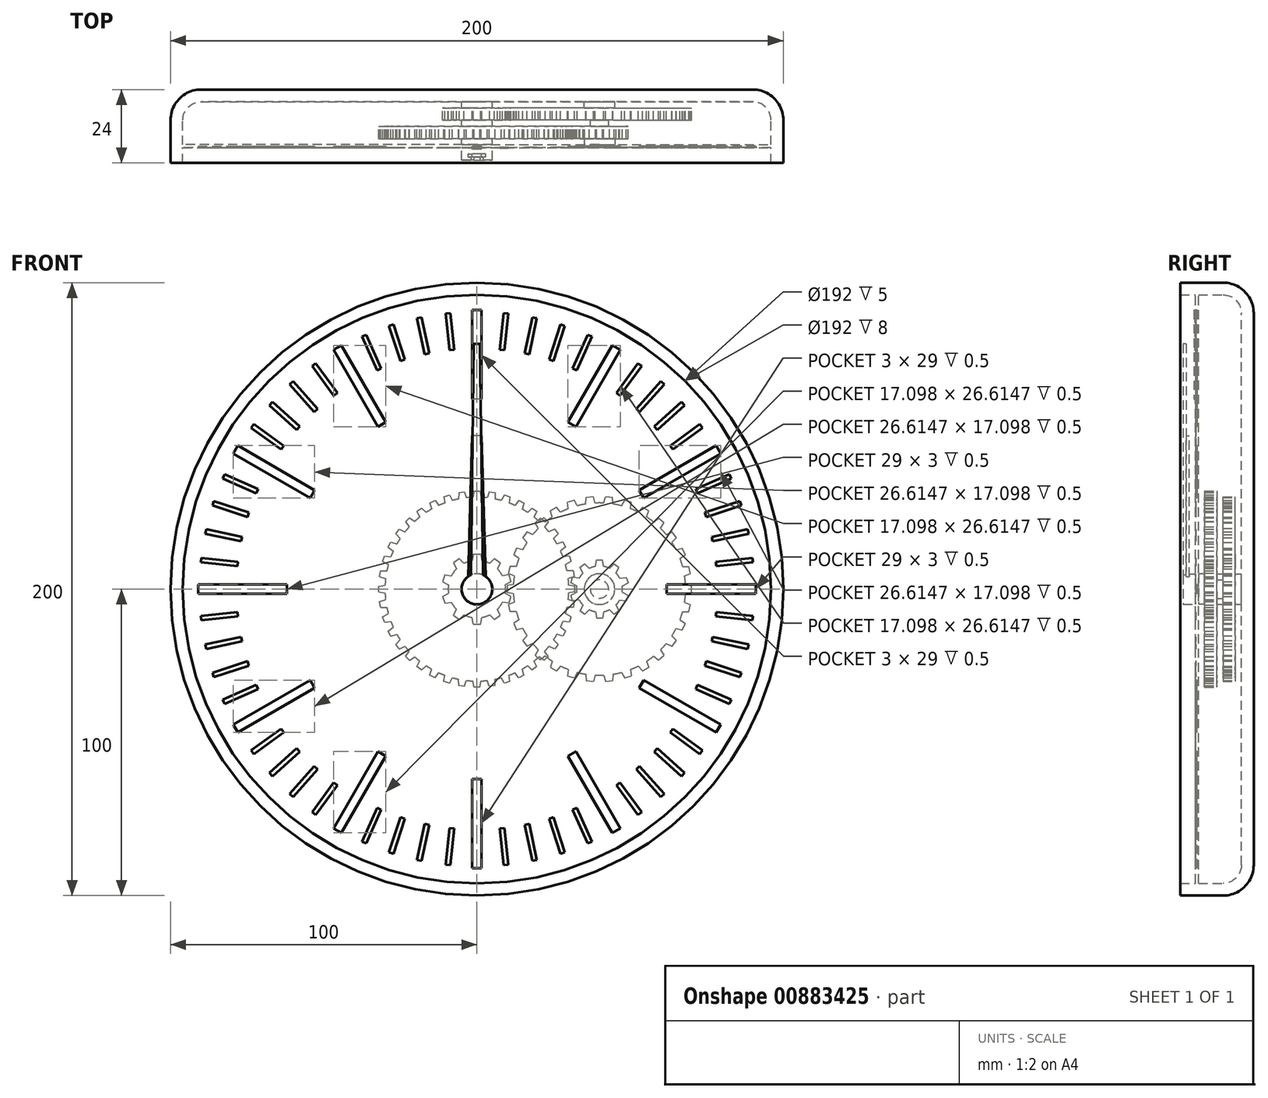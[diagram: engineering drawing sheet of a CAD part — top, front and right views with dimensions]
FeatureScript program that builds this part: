
annotation { "Feature Type Name" : "Feature", "Feature Type Description" : "" }
export const myFeature = defineFeature(function(context is Context, id is Id, definition is map)
    precondition{}
    {
        {
            var Q0;
            Q0=qCreatedBy(makeId("Front.planeOp"),FACE);
            var sketch = newSketch(context, id + "F0", { "sketchPlane" : qUnion([Q0])});
            skCircle(sketch, "E0", {"center": v(0, 0) * mm, "radius": 100 * mm});
            skSolve(sketch);
        }
        {
            var Q0;
            Q0 = qSketchRegion(id + "F0", true);
            extrude(context, id + "F1", {"entities" : qUnion([Q0]), "depth" : 24 * mm, "offsetDistance" : 25 * mm});
        }
        {
            var Q0;
            Q0=makeQuery(id+"F1.opExtrude","CAP_EDGE",EDGE,{"disambiguationData":[OSD([sQuery(id+"F0.wireOp",EDGE,"E0")])],"isStart":true});
            fillet(context, id + "F2", {"entities" : qUnion([Q0]), "radius" : 10 * mm, "tangentPropagation" : true, "allowEdgeOverflow" : false});
        }
        {
            var Q0;
            Q0=makeQuery(id+"F1.opExtrude","CAP_FACE",FACE,{"disambiguationData":[OSD([sQuery(id+"F0.wireOp",EDGE,"E0")])],"isStart":false});
            shell(context, id + "F3", {"entities" : qUnion([Q0]), "thickness" : 4 * mm});
        }
        {
            var Q0;
            {var subQ0=sQuery(id+"F0.wireOp",EDGE,"E0");Q0=makeQuery(id+"F3.opShell","OFFSET_FACE",FACE,{"disambiguationData":[OSD([subQ0]),TDD([makeQuery(id+"F1.opExtrude","CAP_FACE",FACE,{"disambiguationData":[OSD([subQ0])],"isStart":true})])]});}
            var sketch = newSketch(context, id + "F4", { "sketchPlane" : qUnion([Q0])});
            skCircle(sketch, "E1", {"center": v(0, 0) * mm, "radius": 3 * mm});
            skCircle(sketch, "E2", {"center": v(0, 0) * mm, "radius": 5 * mm});
            skCircle(sketch, "E3", {"center": v(40, 0) * mm, "radius": 3 * mm});
            skCircle(sketch, "E4", {"center": v(40, 0) * mm, "radius": 5 * mm});
            skSolve(sketch);
        }
        {
            var Q0;
            Q0 = qSketchRegion(id + "F4", true);
            extrude(context, id + "F5", {"entities" : qUnion([Q0]), "operationType" : NewBodyOperationType.ADD, "depth" : 2 * mm, "offsetDistance" : 25 * mm});
        }
        {
            var Q0;
            {var subQ0=sQuery(id+"F0.wireOp",EDGE,"E0");Q0=makeQuery(id+"F5.boolean.opBoolean","SPLIT",FACE,{"disambiguationData":[TD([makeQuery(id+"F5.opExtrude","SWEPT_FACE",FACE,{"disambiguationData":[OSD([sQuery(id+"F4.wireOp",EDGE,"E1")])]})])],"derivedFrom":makeQuery(id+"F3.opShell","OFFSET_FACE",FACE,{"disambiguationData":[OSD([subQ0]),TDD([makeQuery(id+"F1.opExtrude","CAP_FACE",FACE,{"disambiguationData":[OSD([subQ0])],"isStart":true})])]})});}
            extrude(context, id + "F6", {"entities" : qUnion([Q0]), "depth" : 19 * mm, "offsetDistance" : 25 * mm});
        }
        {
            var Q0;
            {var subQ0=sQuery(id+"F0.wireOp",EDGE,"E0");Q0=makeQuery(id+"F5.boolean.opBoolean","SPLIT",FACE,{"disambiguationData":[TD([makeQuery(id+"F5.opExtrude","SWEPT_FACE",FACE,{"disambiguationData":[OSD([sQuery(id+"F4.wireOp",EDGE,"E3")])]})])],"derivedFrom":makeQuery(id+"F3.opShell","OFFSET_FACE",FACE,{"disambiguationData":[OSD([subQ0]),TDD([makeQuery(id+"F1.opExtrude","CAP_FACE",FACE,{"disambiguationData":[OSD([subQ0])],"isStart":true})])]})});}
            extrude(context, id + "F7", {"entities" : qUnion([Q0]), "depth" : 8 * mm, "offsetDistance" : 25 * mm});
        }
        {
            var Q0;
            Q0=makeQuery(id+"F5.opExtrude","CAP_FACE",FACE,{"disambiguationData":[OSD([sQuery(id+"F4.wireOp",EDGE,"E1"),sQuery(id+"F4.wireOp",EDGE,"E2")])],"isStart":false});
            var sketch = newSketch(context, id + "F8", { "sketchPlane" : qUnion([Q0])});
            skCircle(sketch, "E5", {"center": v(0, 0) * mm, "radius": 9.38 * mm});
            skLineSegment(sketch, "E6", {"start": v(0, 11.38) * mm, "end": v(1.18, 11.38) * mm});
            skLineSegment(sketch, "E7", {"start": v(1.18, 11.38) * mm, "end": v(1.55, 9.25) * mm});
            skLineSegment(sketch, "E8.MirrorCS", {"start": v(0, 11.38) * mm, "end": v(-1.18, 11.38) * mm});
            skLineSegment(sketch, "E9.MirrorCS", {"start": v(-1.18, 11.38) * mm, "end": v(-1.55, 9.25) * mm});
            skLineSegment(sketch, "E10.1.0", {"start": v(-7.64, 8.51) * mm, "end": v(-6.7, 6.57) * mm});
            skLineSegment(sketch, "E10.1.1", {"start": v(-6.69, 9.2) * mm, "end": v(-7.64, 8.51) * mm});
            skLineSegment(sketch, "E10.1.2", {"start": v(-6.69, 9.2) * mm, "end": v(-5.73, 9.9) * mm});
            skLineSegment(sketch, "E10.1.3", {"start": v(-5.73, 9.9) * mm, "end": v(-4.18, 8.4) * mm});
            skLineSegment(sketch, "E10.2.0", {"start": v(-11.18, 2.4) * mm, "end": v(-9.27, 1.38) * mm});
            skLineSegment(sketch, "E10.2.1", {"start": v(-10.82, 3.52) * mm, "end": v(-11.18, 2.4) * mm});
            skLineSegment(sketch, "E10.2.2", {"start": v(-10.82, 3.52) * mm, "end": v(-10.45, 4.64) * mm});
            skLineSegment(sketch, "E10.2.3", {"start": v(-10.45, 4.64) * mm, "end": v(-8.31, 4.33) * mm});
            skLineSegment(sketch, "E11.2.3.0", {"start": v(-10.45, -4.64) * mm, "end": v(-8.31, -4.33) * mm});
            skLineSegment(sketch, "E11.3.3.0", {"start": v(-10.82, -3.52) * mm, "end": v(-10.45, -4.64) * mm});
            skLineSegment(sketch, "E11.6.3.0", {"start": v(-10.82, -3.52) * mm, "end": v(-11.18, -2.4) * mm});
            skLineSegment(sketch, "E11.9.3.0", {"start": v(-11.18, -2.4) * mm, "end": v(-9.27, -1.38) * mm});
            skLineSegment(sketch, "E11.2.4.0", {"start": v(-5.73, -9.9) * mm, "end": v(-4.18, -8.4) * mm});
            skLineSegment(sketch, "E11.3.4.0", {"start": v(-6.69, -9.2) * mm, "end": v(-5.73, -9.9) * mm});
            skLineSegment(sketch, "E11.6.4.0", {"start": v(-6.69, -9.2) * mm, "end": v(-7.64, -8.51) * mm});
            skLineSegment(sketch, "E11.9.4.0", {"start": v(-7.64, -8.51) * mm, "end": v(-6.7, -6.57) * mm});
            skLineSegment(sketch, "E11.2.5.0", {"start": v(1.18, -11.38) * mm, "end": v(1.55, -9.25) * mm});
            skLineSegment(sketch, "E11.3.5.0", {"start": v(0, -11.38) * mm, "end": v(1.18, -11.38) * mm});
            skLineSegment(sketch, "E11.6.5.0", {"start": v(0, -11.38) * mm, "end": v(-1.18, -11.38) * mm});
            skLineSegment(sketch, "E11.9.5.0", {"start": v(-1.18, -11.38) * mm, "end": v(-1.55, -9.25) * mm});
            skLineSegment(sketch, "E11.2.6.0", {"start": v(7.64, -8.51) * mm, "end": v(6.7, -6.57) * mm});
            skLineSegment(sketch, "E11.3.6.0", {"start": v(6.69, -9.2) * mm, "end": v(7.64, -8.51) * mm});
            skLineSegment(sketch, "E11.6.6.0", {"start": v(6.69, -9.2) * mm, "end": v(5.73, -9.9) * mm});
            skLineSegment(sketch, "E11.9.6.0", {"start": v(5.73, -9.9) * mm, "end": v(4.18, -8.4) * mm});
            skLineSegment(sketch, "E11.2.7.0", {"start": v(11.18, -2.4) * mm, "end": v(9.27, -1.38) * mm});
            skLineSegment(sketch, "E11.3.7.0", {"start": v(10.82, -3.52) * mm, "end": v(11.18, -2.4) * mm});
            skLineSegment(sketch, "E11.6.7.0", {"start": v(10.82, -3.52) * mm, "end": v(10.45, -4.64) * mm});
            skLineSegment(sketch, "E11.9.7.0", {"start": v(10.45, -4.64) * mm, "end": v(8.31, -4.33) * mm});
            skLineSegment(sketch, "E11.2.8.0", {"start": v(10.45, 4.64) * mm, "end": v(8.31, 4.33) * mm});
            skLineSegment(sketch, "E11.3.8.0", {"start": v(10.82, 3.52) * mm, "end": v(10.45, 4.64) * mm});
            skLineSegment(sketch, "E11.6.8.0", {"start": v(10.82, 3.52) * mm, "end": v(11.18, 2.4) * mm});
            skLineSegment(sketch, "E11.9.8.0", {"start": v(11.18, 2.4) * mm, "end": v(9.27, 1.38) * mm});
            skLineSegment(sketch, "E11.2.9.0", {"start": v(5.73, 9.9) * mm, "end": v(4.18, 8.4) * mm});
            skLineSegment(sketch, "E11.3.9.0", {"start": v(6.69, 9.2) * mm, "end": v(5.73, 9.9) * mm});
            skLineSegment(sketch, "E11.6.9.0", {"start": v(6.69, 9.2) * mm, "end": v(7.64, 8.51) * mm});
            skLineSegment(sketch, "E11.9.9.0", {"start": v(7.64, 8.51) * mm, "end": v(6.7, 6.57) * mm});
            skSolve(sketch);
        }
        {
            var Q0;
            Q0 = qSketchRegion(id + "F8", true);
            extrude(context, id + "F9", {"entities" : qUnion([Q0]), "operationType" : NewBodyOperationType.ADD, "depth" : 4 * mm, "offsetDistance" : 25 * mm});
        }
        {
            var Q0;
            Q0=makeQuery(id+"F5.opExtrude","CAP_FACE",FACE,{"disambiguationData":[OSD([sQuery(id+"F4.wireOp",EDGE,"E3"),sQuery(id+"F4.wireOp",EDGE,"E4")])],"isStart":false});
            var sketch = newSketch(context, id + "F10", { "sketchPlane" : qUnion([Q0])});
            skCircle(sketch, "E12", {"center": v(40, 0) * mm, "radius": 28.13 * mm});
            skLineSegment(sketch, "E13", {"start": v(11.92, 1.54) * mm, "end": v(9.88, 1.18) * mm});
            skLineSegment(sketch, "E14", {"start": v(9.88, 1.18) * mm, "end": v(9.88, 0) * mm});
            skLineSegment(sketch, "E15.MirrorCS", {"start": v(9.88, -1.18) * mm, "end": v(9.88, 0) * mm});
            skLineSegment(sketch, "E16.MirrorCS", {"start": v(11.92, -1.54) * mm, "end": v(9.88, -1.18) * mm});
            skLineSegment(sketch, "E17.1.0", {"start": v(12.21, -4.33) * mm, "end": v(10.29, -5.11) * mm});
            skLineSegment(sketch, "E17.1.1", {"start": v(10.29, -5.11) * mm, "end": v(10.53, -6.26) * mm});
            skLineSegment(sketch, "E17.1.2", {"start": v(10.78, -7.42) * mm, "end": v(10.53, -6.26) * mm});
            skLineSegment(sketch, "E17.1.3", {"start": v(12.85, -7.34) * mm, "end": v(10.78, -7.42) * mm});
            skLineSegment(sketch, "E17.2.0", {"start": v(13.72, -10.02) * mm, "end": v(12, -11.18) * mm});
            skLineSegment(sketch, "E17.2.1", {"start": v(12, -11.18) * mm, "end": v(12.48, -12.25) * mm});
            skLineSegment(sketch, "E17.2.2", {"start": v(12.96, -13.33) * mm, "end": v(12.48, -12.25) * mm});
            skLineSegment(sketch, "E17.2.3", {"start": v(14.97, -12.83) * mm, "end": v(12.96, -13.33) * mm});
            skLineSegment(sketch, "E18.2.3.0", {"start": v(16.38, -15.26) * mm, "end": v(14.94, -16.75) * mm});
            skLineSegment(sketch, "E18.3.3.0", {"start": v(14.94, -16.75) * mm, "end": v(15.63, -17.7) * mm});
            skLineSegment(sketch, "E18.6.3.0", {"start": v(16.32, -18.66) * mm, "end": v(15.63, -17.7) * mm});
            skLineSegment(sketch, "E18.9.3.0", {"start": v(18.18, -17.75) * mm, "end": v(16.32, -18.66) * mm});
            skLineSegment(sketch, "E18.2.4.0", {"start": v(20.07, -19.84) * mm, "end": v(18.97, -21.6) * mm});
            skLineSegment(sketch, "E18.3.4.0", {"start": v(18.97, -21.6) * mm, "end": v(19.84, -22.39) * mm});
            skLineSegment(sketch, "E18.6.4.0", {"start": v(20.72, -23.18) * mm, "end": v(19.84, -22.39) * mm});
            skLineSegment(sketch, "E18.9.4.0", {"start": v(22.35, -21.9) * mm, "end": v(20.72, -23.18) * mm});
            skLineSegment(sketch, "E18.2.5.0", {"start": v(24.63, -23.55) * mm, "end": v(23.92, -25.5) * mm});
            skLineSegment(sketch, "E18.3.5.0", {"start": v(23.92, -25.5) * mm, "end": v(24.94, -26.09) * mm});
            skLineSegment(sketch, "E18.6.5.0", {"start": v(25.96, -26.68) * mm, "end": v(24.94, -26.09) * mm});
            skLineSegment(sketch, "E18.9.5.0", {"start": v(27.3, -25.09) * mm, "end": v(25.96, -26.68) * mm});
            skLineSegment(sketch, "E18.2.6.0", {"start": v(29.86, -26.23) * mm, "end": v(29.57, -28.29) * mm});
            skLineSegment(sketch, "E18.3.6.0", {"start": v(29.57, -28.29) * mm, "end": v(30.7, -28.65) * mm});
            skLineSegment(sketch, "E18.6.6.0", {"start": v(31.81, -29.01) * mm, "end": v(30.7, -28.65) * mm});
            skLineSegment(sketch, "E18.9.6.0", {"start": v(32.78, -27.18) * mm, "end": v(31.81, -29.01) * mm});
            skLineSegment(sketch, "E18.2.7.0", {"start": v(35.53, -27.77) * mm, "end": v(35.68, -29.84) * mm});
            skLineSegment(sketch, "E18.3.7.0", {"start": v(35.68, -29.84) * mm, "end": v(36.85, -29.96) * mm});
            skLineSegment(sketch, "E18.6.7.0", {"start": v(38.02, -30.08) * mm, "end": v(36.85, -29.96) * mm});
            skLineSegment(sketch, "E18.9.7.0", {"start": v(38.6, -28.09) * mm, "end": v(38.02, -30.08) * mm});
            skLineSegment(sketch, "E18.2.8.0", {"start": v(41.4, -28.09) * mm, "end": v(41.98, -30.08) * mm});
            skLineSegment(sketch, "E18.3.8.0", {"start": v(41.98, -30.08) * mm, "end": v(43.15, -29.96) * mm});
            skLineSegment(sketch, "E18.6.8.0", {"start": v(44.32, -29.84) * mm, "end": v(43.15, -29.96) * mm});
            skLineSegment(sketch, "E18.9.8.0", {"start": v(44.47, -27.77) * mm, "end": v(44.32, -29.84) * mm});
            skLineSegment(sketch, "E18.2.9.0", {"start": v(47.22, -27.18) * mm, "end": v(48.19, -29.01) * mm});
            skLineSegment(sketch, "E18.3.9.0", {"start": v(48.19, -29.01) * mm, "end": v(49.3, -28.65) * mm});
            skLineSegment(sketch, "E18.6.9.0", {"start": v(50.43, -28.29) * mm, "end": v(49.3, -28.65) * mm});
            skLineSegment(sketch, "E18.9.9.0", {"start": v(50.14, -26.23) * mm, "end": v(50.43, -28.29) * mm});
            skLineSegment(sketch, "E18.2.10.0", {"start": v(52.7, -25.09) * mm, "end": v(54.04, -26.68) * mm});
            skLineSegment(sketch, "E18.3.10.0", {"start": v(54.04, -26.68) * mm, "end": v(55.06, -26.09) * mm});
            skLineSegment(sketch, "E18.6.10.0", {"start": v(56.08, -25.5) * mm, "end": v(55.06, -26.09) * mm});
            skLineSegment(sketch, "E18.9.10.0", {"start": v(55.37, -23.55) * mm, "end": v(56.08, -25.5) * mm});
            skLineSegment(sketch, "E18.2.11.0", {"start": v(57.65, -21.9) * mm, "end": v(59.28, -23.18) * mm});
            skLineSegment(sketch, "E18.3.11.0", {"start": v(59.28, -23.18) * mm, "end": v(60.16, -22.39) * mm});
            skLineSegment(sketch, "E18.6.11.0", {"start": v(61.03, -21.6) * mm, "end": v(60.16, -22.39) * mm});
            skLineSegment(sketch, "E18.9.11.0", {"start": v(59.93, -19.84) * mm, "end": v(61.03, -21.6) * mm});
            skLineSegment(sketch, "E18.2.12.0", {"start": v(61.82, -17.75) * mm, "end": v(63.68, -18.66) * mm});
            skLineSegment(sketch, "E18.3.12.0", {"start": v(63.68, -18.66) * mm, "end": v(64.37, -17.7) * mm});
            skLineSegment(sketch, "E18.6.12.0", {"start": v(65.06, -16.75) * mm, "end": v(64.37, -17.7) * mm});
            skLineSegment(sketch, "E18.9.12.0", {"start": v(63.62, -15.26) * mm, "end": v(65.06, -16.75) * mm});
            skLineSegment(sketch, "E18.2.13.0", {"start": v(65.03, -12.83) * mm, "end": v(67.04, -13.33) * mm});
            skLineSegment(sketch, "E18.3.13.0", {"start": v(67.04, -13.33) * mm, "end": v(67.52, -12.25) * mm});
            skLineSegment(sketch, "E18.6.13.0", {"start": v(68, -11.18) * mm, "end": v(67.52, -12.25) * mm});
            skLineSegment(sketch, "E18.9.13.0", {"start": v(66.28, -10.02) * mm, "end": v(68, -11.18) * mm});
            skLineSegment(sketch, "E18.2.14.0", {"start": v(67.15, -7.34) * mm, "end": v(69.22, -7.42) * mm});
            skLineSegment(sketch, "E18.3.14.0", {"start": v(69.22, -7.42) * mm, "end": v(69.47, -6.26) * mm});
            skLineSegment(sketch, "E18.6.14.0", {"start": v(69.71, -5.11) * mm, "end": v(69.47, -6.26) * mm});
            skLineSegment(sketch, "E18.9.14.0", {"start": v(67.79, -4.33) * mm, "end": v(69.71, -5.11) * mm});
            skLineSegment(sketch, "E18.2.15.0", {"start": v(68.08, -1.54) * mm, "end": v(70.13, -1.18) * mm});
            skLineSegment(sketch, "E18.3.15.0", {"start": v(70.12, -1.18) * mm, "end": v(70.12, 0) * mm});
            skLineSegment(sketch, "E18.6.15.0", {"start": v(70.12, 1.18) * mm, "end": v(70.12, 0) * mm});
            skLineSegment(sketch, "E18.9.15.0", {"start": v(68.08, 1.54) * mm, "end": v(70.13, 1.18) * mm});
            skLineSegment(sketch, "E18.2.16.0", {"start": v(67.79, 4.33) * mm, "end": v(69.71, 5.11) * mm});
            skLineSegment(sketch, "E18.3.16.0", {"start": v(69.71, 5.11) * mm, "end": v(69.47, 6.26) * mm});
            skLineSegment(sketch, "E18.6.16.0", {"start": v(69.22, 7.42) * mm, "end": v(69.47, 6.26) * mm});
            skLineSegment(sketch, "E18.9.16.0", {"start": v(67.15, 7.34) * mm, "end": v(69.22, 7.42) * mm});
            skLineSegment(sketch, "E18.2.17.0", {"start": v(66.28, 10.02) * mm, "end": v(68, 11.18) * mm});
            skLineSegment(sketch, "E18.3.17.0", {"start": v(68, 11.18) * mm, "end": v(67.52, 12.25) * mm});
            skLineSegment(sketch, "E18.6.17.0", {"start": v(67.04, 13.33) * mm, "end": v(67.52, 12.25) * mm});
            skLineSegment(sketch, "E18.9.17.0", {"start": v(65.03, 12.83) * mm, "end": v(67.04, 13.33) * mm});
            skLineSegment(sketch, "E18.2.18.0", {"start": v(63.62, 15.26) * mm, "end": v(65.06, 16.75) * mm});
            skLineSegment(sketch, "E18.3.18.0", {"start": v(65.06, 16.75) * mm, "end": v(64.37, 17.7) * mm});
            skLineSegment(sketch, "E18.6.18.0", {"start": v(63.68, 18.66) * mm, "end": v(64.37, 17.7) * mm});
            skLineSegment(sketch, "E18.9.18.0", {"start": v(61.82, 17.75) * mm, "end": v(63.68, 18.66) * mm});
            skLineSegment(sketch, "E18.2.19.0", {"start": v(59.93, 19.84) * mm, "end": v(61.03, 21.6) * mm});
            skLineSegment(sketch, "E18.3.19.0", {"start": v(61.03, 21.6) * mm, "end": v(60.16, 22.39) * mm});
            skLineSegment(sketch, "E18.6.19.0", {"start": v(59.28, 23.18) * mm, "end": v(60.16, 22.39) * mm});
            skLineSegment(sketch, "E18.9.19.0", {"start": v(57.65, 21.9) * mm, "end": v(59.28, 23.18) * mm});
            skLineSegment(sketch, "E18.2.20.0", {"start": v(55.37, 23.55) * mm, "end": v(56.08, 25.5) * mm});
            skLineSegment(sketch, "E18.3.20.0", {"start": v(56.08, 25.5) * mm, "end": v(55.06, 26.09) * mm});
            skLineSegment(sketch, "E18.6.20.0", {"start": v(54.04, 26.68) * mm, "end": v(55.06, 26.09) * mm});
            skLineSegment(sketch, "E18.9.20.0", {"start": v(52.7, 25.09) * mm, "end": v(54.04, 26.68) * mm});
            skLineSegment(sketch, "E18.2.21.0", {"start": v(50.14, 26.23) * mm, "end": v(50.43, 28.29) * mm});
            skLineSegment(sketch, "E18.3.21.0", {"start": v(50.43, 28.29) * mm, "end": v(49.3, 28.65) * mm});
            skLineSegment(sketch, "E18.6.21.0", {"start": v(48.19, 29.01) * mm, "end": v(49.3, 28.65) * mm});
            skLineSegment(sketch, "E18.9.21.0", {"start": v(47.22, 27.18) * mm, "end": v(48.19, 29.01) * mm});
            skLineSegment(sketch, "E18.2.22.0", {"start": v(44.47, 27.77) * mm, "end": v(44.32, 29.84) * mm});
            skLineSegment(sketch, "E18.3.22.0", {"start": v(44.32, 29.84) * mm, "end": v(43.15, 29.96) * mm});
            skLineSegment(sketch, "E18.6.22.0", {"start": v(41.98, 30.08) * mm, "end": v(43.15, 29.96) * mm});
            skLineSegment(sketch, "E18.9.22.0", {"start": v(41.4, 28.09) * mm, "end": v(41.98, 30.08) * mm});
            skLineSegment(sketch, "E18.2.23.0", {"start": v(38.6, 28.09) * mm, "end": v(38.02, 30.08) * mm});
            skLineSegment(sketch, "E18.3.23.0", {"start": v(38.02, 30.08) * mm, "end": v(36.85, 29.96) * mm});
            skLineSegment(sketch, "E18.6.23.0", {"start": v(35.68, 29.84) * mm, "end": v(36.85, 29.96) * mm});
            skLineSegment(sketch, "E18.9.23.0", {"start": v(35.53, 27.77) * mm, "end": v(35.68, 29.84) * mm});
            skLineSegment(sketch, "E18.2.24.0", {"start": v(32.78, 27.18) * mm, "end": v(31.81, 29.01) * mm});
            skLineSegment(sketch, "E18.3.24.0", {"start": v(31.81, 29.01) * mm, "end": v(30.7, 28.65) * mm});
            skLineSegment(sketch, "E18.6.24.0", {"start": v(29.57, 28.29) * mm, "end": v(30.7, 28.65) * mm});
            skLineSegment(sketch, "E18.9.24.0", {"start": v(29.86, 26.23) * mm, "end": v(29.57, 28.29) * mm});
            skLineSegment(sketch, "E18.2.25.0", {"start": v(27.3, 25.09) * mm, "end": v(25.96, 26.68) * mm});
            skLineSegment(sketch, "E18.3.25.0", {"start": v(25.96, 26.68) * mm, "end": v(24.94, 26.09) * mm});
            skLineSegment(sketch, "E18.6.25.0", {"start": v(23.92, 25.5) * mm, "end": v(24.94, 26.09) * mm});
            skLineSegment(sketch, "E18.9.25.0", {"start": v(24.63, 23.55) * mm, "end": v(23.92, 25.5) * mm});
            skLineSegment(sketch, "E18.2.26.0", {"start": v(22.35, 21.9) * mm, "end": v(20.72, 23.18) * mm});
            skLineSegment(sketch, "E18.3.26.0", {"start": v(20.72, 23.18) * mm, "end": v(19.84, 22.39) * mm});
            skLineSegment(sketch, "E18.6.26.0", {"start": v(18.97, 21.6) * mm, "end": v(19.84, 22.39) * mm});
            skLineSegment(sketch, "E18.9.26.0", {"start": v(20.07, 19.84) * mm, "end": v(18.97, 21.6) * mm});
            skLineSegment(sketch, "E18.2.27.0", {"start": v(18.18, 17.75) * mm, "end": v(16.32, 18.66) * mm});
            skLineSegment(sketch, "E18.3.27.0", {"start": v(16.32, 18.66) * mm, "end": v(15.63, 17.7) * mm});
            skLineSegment(sketch, "E18.6.27.0", {"start": v(14.94, 16.75) * mm, "end": v(15.63, 17.7) * mm});
            skLineSegment(sketch, "E18.9.27.0", {"start": v(16.38, 15.26) * mm, "end": v(14.94, 16.75) * mm});
            skLineSegment(sketch, "E18.2.28.0", {"start": v(14.97, 12.83) * mm, "end": v(12.96, 13.33) * mm});
            skLineSegment(sketch, "E18.3.28.0", {"start": v(12.96, 13.33) * mm, "end": v(12.48, 12.25) * mm});
            skLineSegment(sketch, "E18.6.28.0", {"start": v(12, 11.18) * mm, "end": v(12.48, 12.25) * mm});
            skLineSegment(sketch, "E18.9.28.0", {"start": v(13.72, 10.02) * mm, "end": v(12, 11.18) * mm});
            skLineSegment(sketch, "E18.2.29.0", {"start": v(12.85, 7.34) * mm, "end": v(10.78, 7.42) * mm});
            skLineSegment(sketch, "E18.3.29.0", {"start": v(10.78, 7.42) * mm, "end": v(10.53, 6.26) * mm});
            skLineSegment(sketch, "E18.6.29.0", {"start": v(10.29, 5.11) * mm, "end": v(10.53, 6.26) * mm});
            skLineSegment(sketch, "E18.9.29.0", {"start": v(12.21, 4.33) * mm, "end": v(10.29, 5.11) * mm});
            skSolve(sketch);
        }
        {
            var Q0;
            Q0 = qSketchRegion(id + "F10", true);
            extrude(context, id + "F11", {"entities" : qUnion([Q0]), "operationType" : NewBodyOperationType.ADD, "depth" : 4 * mm, "offsetDistance" : 25 * mm});
        }
        {
            var Q0;
            Q0=makeQuery(id+"F9.opExtrude","CAP_FACE",FACE,{"disambiguationData":[OSD([sQuery(id+"F8.wireOp",EDGE,"E5"),sQuery(id+"F8.wireOp",EDGE,"E6"),sQuery(id+"F8.wireOp",EDGE,"E7"),sQuery(id+"F8.wireOp",EDGE,"E8.MirrorCS"),sQuery(id+"F8.wireOp",EDGE,"E9.MirrorCS"),sQuery(id+"F8.wireOp",EDGE,"E10.1.0"),sQuery(id+"F8.wireOp",EDGE,"E10.1.1"),sQuery(id+"F8.wireOp",EDGE,"E10.1.2"),sQuery(id+"F8.wireOp",EDGE,"E10.1.3"),sQuery(id+"F8.wireOp",EDGE,"E10.2.0"),sQuery(id+"F8.wireOp",EDGE,"E10.2.1"),sQuery(id+"F8.wireOp",EDGE,"E10.2.2"),sQuery(id+"F8.wireOp",EDGE,"E10.2.3"),sQuery(id+"F8.wireOp",EDGE,"E11.2.3.0"),sQuery(id+"F8.wireOp",EDGE,"E11.3.3.0"),sQuery(id+"F8.wireOp",EDGE,"E11.6.3.0"),sQuery(id+"F8.wireOp",EDGE,"E11.9.3.0"),sQuery(id+"F8.wireOp",EDGE,"E11.2.4.0"),sQuery(id+"F8.wireOp",EDGE,"E11.3.4.0"),sQuery(id+"F8.wireOp",EDGE,"E11.6.4.0"),sQuery(id+"F8.wireOp",EDGE,"E11.9.4.0"),sQuery(id+"F8.wireOp",EDGE,"E11.2.5.0"),sQuery(id+"F8.wireOp",EDGE,"E11.3.5.0"),sQuery(id+"F8.wireOp",EDGE,"E11.6.5.0"),sQuery(id+"F8.wireOp",EDGE,"E11.9.5.0"),sQuery(id+"F8.wireOp",EDGE,"E11.2.6.0"),sQuery(id+"F8.wireOp",EDGE,"E11.3.6.0"),sQuery(id+"F8.wireOp",EDGE,"E11.6.6.0"),sQuery(id+"F8.wireOp",EDGE,"E11.9.6.0"),sQuery(id+"F8.wireOp",EDGE,"E11.2.7.0"),sQuery(id+"F8.wireOp",EDGE,"E11.3.7.0"),sQuery(id+"F8.wireOp",EDGE,"E11.6.7.0"),sQuery(id+"F8.wireOp",EDGE,"E11.9.7.0"),sQuery(id+"F8.wireOp",EDGE,"E11.2.8.0"),sQuery(id+"F8.wireOp",EDGE,"E11.3.8.0"),sQuery(id+"F8.wireOp",EDGE,"E11.6.8.0"),sQuery(id+"F8.wireOp",EDGE,"E11.9.8.0"),sQuery(id+"F8.wireOp",EDGE,"E11.2.9.0"),sQuery(id+"F8.wireOp",EDGE,"E11.3.9.0"),sQuery(id+"F8.wireOp",EDGE,"E11.6.9.0"),sQuery(id+"F8.wireOp",EDGE,"E11.9.9.0")])],"isStart":false});
            var sketch = newSketch(context, id + "F12", { "sketchPlane" : qUnion([Q0])});
            skCircle(sketch, "E19.0", {"center": v(0, 0) * mm, "radius": 3 * mm});
            skCircle(sketch, "E20.0", {"center": v(0, 0) * mm, "radius": 5 * mm});
            skSolve(sketch);
        }
        {
            var Q0;
            Q0 = qSketchRegion(id + "F12", true);
            extrude(context, id + "F13", {"entities" : qUnion([Q0]), "depth" : 2 * mm, "offsetDistance" : 25 * mm});
        }
        {
            var Q0;
            Q0=makeQuery(id+"F13.opExtrude","CAP_FACE",FACE,{"disambiguationData":[OSD([sQuery(id+"F12.wireOp",EDGE,"E19.0"),sQuery(id+"F12.wireOp",EDGE,"E20.0")])],"isStart":false});
            var sketch = newSketch(context, id + "F14", { "sketchPlane" : qUnion([Q0])});
            skCircle(sketch, "E21.0", {"center": v(0, 0) * mm, "radius": 3 * mm});
            skCircle(sketch, "E22", {"center": v(0, 0) * mm, "radius": 30 * mm});
            skLineSegment(sketch, "E23", {"start": v(0, 32) * mm, "end": v(0.94, 32) * mm});
            skLineSegment(sketch, "E24", {"start": v(0.94, 32) * mm, "end": v(1.3, 29.97) * mm});
            skLineSegment(sketch, "E25.MirrorCS", {"start": v(0, 32) * mm, "end": v(-0.94, 32) * mm});
            skLineSegment(sketch, "E26.MirrorCS", {"start": v(-0.94, 32) * mm, "end": v(-1.3, 29.97) * mm});
            skLineSegment(sketch, "E27.1.0", {"start": v(-4.08, 31.75) * mm, "end": v(-3.4, 29.8) * mm});
            skLineSegment(sketch, "E27.1.1", {"start": v(-5, 31.6) * mm, "end": v(-4.08, 31.75) * mm});
            skLineSegment(sketch, "E27.1.2", {"start": v(-5, 31.6) * mm, "end": v(-5.94, 31.46) * mm});
            skLineSegment(sketch, "E27.1.3", {"start": v(-5.94, 31.46) * mm, "end": v(-5.97, 29.4) * mm});
            skLineSegment(sketch, "E27.2.0", {"start": v(-9, 30.73) * mm, "end": v(-8.03, 28.9) * mm});
            skLineSegment(sketch, "E27.2.1", {"start": v(-9.89, 30.43) * mm, "end": v(-9, 30.73) * mm});
            skLineSegment(sketch, "E27.2.2", {"start": v(-9.89, 30.43) * mm, "end": v(-10.78, 30.14) * mm});
            skLineSegment(sketch, "E27.2.3", {"start": v(-10.78, 30.14) * mm, "end": v(-10.5, 28.1) * mm});
            skLineSegment(sketch, "E28.2.3.0", {"start": v(-13.69, 28.94) * mm, "end": v(-12.45, 27.3) * mm});
            skLineSegment(sketch, "E28.3.3.0", {"start": v(-14.53, 28.51) * mm, "end": v(-13.69, 28.94) * mm});
            skLineSegment(sketch, "E28.6.3.0", {"start": v(-14.53, 28.51) * mm, "end": v(-15.37, 28.08) * mm});
            skLineSegment(sketch, "E28.9.3.0", {"start": v(-15.37, 28.08) * mm, "end": v(-14.77, 26.11) * mm});
            skLineSegment(sketch, "E28.2.4.0", {"start": v(-18.05, 26.44) * mm, "end": v(-16.57, 25.01) * mm});
            skLineSegment(sketch, "E28.3.4.0", {"start": v(-18.8, 25.89) * mm, "end": v(-18.05, 26.44) * mm});
            skLineSegment(sketch, "E28.6.4.0", {"start": v(-18.8, 25.89) * mm, "end": v(-19.57, 25.33) * mm});
            skLineSegment(sketch, "E28.9.4.0", {"start": v(-19.57, 25.33) * mm, "end": v(-18.67, 23.48) * mm});
            skLineSegment(sketch, "E28.2.5.0", {"start": v(-21.96, 23.3) * mm, "end": v(-20.27, 22.11) * mm});
            skLineSegment(sketch, "E28.3.5.0", {"start": v(-22.63, 22.63) * mm, "end": v(-21.96, 23.3) * mm});
            skLineSegment(sketch, "E28.6.5.0", {"start": v(-22.63, 22.63) * mm, "end": v(-23.3, 21.96) * mm});
            skLineSegment(sketch, "E28.9.5.0", {"start": v(-23.3, 21.96) * mm, "end": v(-22.11, 20.27) * mm});
            skLineSegment(sketch, "E28.2.6.0", {"start": v(-25.33, 19.57) * mm, "end": v(-23.48, 18.67) * mm});
            skLineSegment(sketch, "E28.3.6.0", {"start": v(-25.89, 18.8) * mm, "end": v(-25.33, 19.57) * mm});
            skLineSegment(sketch, "E28.6.6.0", {"start": v(-25.89, 18.8) * mm, "end": v(-26.44, 18.05) * mm});
            skLineSegment(sketch, "E28.9.6.0", {"start": v(-26.44, 18.05) * mm, "end": v(-25.01, 16.57) * mm});
            skLineSegment(sketch, "E28.2.7.0", {"start": v(-28.08, 15.37) * mm, "end": v(-26.11, 14.77) * mm});
            skLineSegment(sketch, "E28.3.7.0", {"start": v(-28.51, 14.53) * mm, "end": v(-28.08, 15.37) * mm});
            skLineSegment(sketch, "E28.6.7.0", {"start": v(-28.51, 14.53) * mm, "end": v(-28.94, 13.69) * mm});
            skLineSegment(sketch, "E28.9.7.0", {"start": v(-28.94, 13.69) * mm, "end": v(-27.3, 12.45) * mm});
            skLineSegment(sketch, "E28.2.8.0", {"start": v(-30.14, 10.78) * mm, "end": v(-28.1, 10.5) * mm});
            skLineSegment(sketch, "E28.3.8.0", {"start": v(-30.43, 9.89) * mm, "end": v(-30.14, 10.78) * mm});
            skLineSegment(sketch, "E28.6.8.0", {"start": v(-30.43, 9.89) * mm, "end": v(-30.73, 9) * mm});
            skLineSegment(sketch, "E28.9.8.0", {"start": v(-30.73, 9) * mm, "end": v(-28.9, 8.03) * mm});
            skLineSegment(sketch, "E28.2.9.0", {"start": v(-31.46, 5.94) * mm, "end": v(-29.4, 5.97) * mm});
            skLineSegment(sketch, "E28.3.9.0", {"start": v(-31.6, 5) * mm, "end": v(-31.46, 5.94) * mm});
            skLineSegment(sketch, "E28.6.9.0", {"start": v(-31.6, 5) * mm, "end": v(-31.75, 4.08) * mm});
            skLineSegment(sketch, "E28.9.9.0", {"start": v(-31.75, 4.08) * mm, "end": v(-29.8, 3.4) * mm});
            skLineSegment(sketch, "E28.2.10.0", {"start": v(-32, 0.94) * mm, "end": v(-29.97, 1.3) * mm});
            skLineSegment(sketch, "E28.3.10.0", {"start": v(-32, 0) * mm, "end": v(-32, 0.94) * mm});
            skLineSegment(sketch, "E28.6.10.0", {"start": v(-32, 0) * mm, "end": v(-32, -0.94) * mm});
            skLineSegment(sketch, "E28.9.10.0", {"start": v(-32, -0.94) * mm, "end": v(-29.97, -1.3) * mm});
            skLineSegment(sketch, "E28.2.11.0", {"start": v(-31.75, -4.08) * mm, "end": v(-29.8, -3.4) * mm});
            skLineSegment(sketch, "E28.3.11.0", {"start": v(-31.6, -5) * mm, "end": v(-31.75, -4.08) * mm});
            skLineSegment(sketch, "E28.6.11.0", {"start": v(-31.6, -5) * mm, "end": v(-31.46, -5.94) * mm});
            skLineSegment(sketch, "E28.9.11.0", {"start": v(-31.46, -5.94) * mm, "end": v(-29.4, -5.97) * mm});
            skLineSegment(sketch, "E28.2.12.0", {"start": v(-30.73, -9) * mm, "end": v(-28.9, -8.03) * mm});
            skLineSegment(sketch, "E28.3.12.0", {"start": v(-30.43, -9.89) * mm, "end": v(-30.73, -9) * mm});
            skLineSegment(sketch, "E28.6.12.0", {"start": v(-30.43, -9.89) * mm, "end": v(-30.14, -10.78) * mm});
            skLineSegment(sketch, "E28.9.12.0", {"start": v(-30.14, -10.78) * mm, "end": v(-28.1, -10.5) * mm});
            skLineSegment(sketch, "E28.2.13.0", {"start": v(-28.94, -13.69) * mm, "end": v(-27.3, -12.45) * mm});
            skLineSegment(sketch, "E28.3.13.0", {"start": v(-28.51, -14.53) * mm, "end": v(-28.94, -13.69) * mm});
            skLineSegment(sketch, "E28.6.13.0", {"start": v(-28.51, -14.53) * mm, "end": v(-28.08, -15.37) * mm});
            skLineSegment(sketch, "E28.9.13.0", {"start": v(-28.08, -15.37) * mm, "end": v(-26.11, -14.77) * mm});
            skLineSegment(sketch, "E28.2.14.0", {"start": v(-26.44, -18.05) * mm, "end": v(-25.01, -16.57) * mm});
            skLineSegment(sketch, "E28.3.14.0", {"start": v(-25.89, -18.8) * mm, "end": v(-26.44, -18.05) * mm});
            skLineSegment(sketch, "E28.6.14.0", {"start": v(-25.89, -18.8) * mm, "end": v(-25.33, -19.57) * mm});
            skLineSegment(sketch, "E28.9.14.0", {"start": v(-25.33, -19.57) * mm, "end": v(-23.48, -18.67) * mm});
            skLineSegment(sketch, "E28.2.15.0", {"start": v(-23.3, -21.96) * mm, "end": v(-22.11, -20.27) * mm});
            skLineSegment(sketch, "E28.3.15.0", {"start": v(-22.63, -22.63) * mm, "end": v(-23.3, -21.96) * mm});
            skLineSegment(sketch, "E28.6.15.0", {"start": v(-22.63, -22.63) * mm, "end": v(-21.96, -23.3) * mm});
            skLineSegment(sketch, "E28.9.15.0", {"start": v(-21.96, -23.3) * mm, "end": v(-20.27, -22.11) * mm});
            skLineSegment(sketch, "E28.2.16.0", {"start": v(-19.57, -25.33) * mm, "end": v(-18.67, -23.48) * mm});
            skLineSegment(sketch, "E28.3.16.0", {"start": v(-18.8, -25.89) * mm, "end": v(-19.57, -25.33) * mm});
            skLineSegment(sketch, "E28.6.16.0", {"start": v(-18.8, -25.89) * mm, "end": v(-18.05, -26.44) * mm});
            skLineSegment(sketch, "E28.9.16.0", {"start": v(-18.05, -26.44) * mm, "end": v(-16.57, -25.01) * mm});
            skLineSegment(sketch, "E28.2.17.0", {"start": v(-15.37, -28.08) * mm, "end": v(-14.77, -26.11) * mm});
            skLineSegment(sketch, "E28.3.17.0", {"start": v(-14.53, -28.51) * mm, "end": v(-15.37, -28.08) * mm});
            skLineSegment(sketch, "E28.6.17.0", {"start": v(-14.53, -28.51) * mm, "end": v(-13.69, -28.94) * mm});
            skLineSegment(sketch, "E28.9.17.0", {"start": v(-13.69, -28.94) * mm, "end": v(-12.45, -27.3) * mm});
            skLineSegment(sketch, "E28.2.18.0", {"start": v(-10.78, -30.14) * mm, "end": v(-10.5, -28.1) * mm});
            skLineSegment(sketch, "E28.3.18.0", {"start": v(-9.89, -30.43) * mm, "end": v(-10.78, -30.14) * mm});
            skLineSegment(sketch, "E28.6.18.0", {"start": v(-9.89, -30.43) * mm, "end": v(-9, -30.73) * mm});
            skLineSegment(sketch, "E28.9.18.0", {"start": v(-9, -30.73) * mm, "end": v(-8.03, -28.9) * mm});
            skLineSegment(sketch, "E28.2.19.0", {"start": v(-5.94, -31.46) * mm, "end": v(-5.97, -29.4) * mm});
            skLineSegment(sketch, "E28.3.19.0", {"start": v(-5, -31.6) * mm, "end": v(-5.94, -31.46) * mm});
            skLineSegment(sketch, "E28.6.19.0", {"start": v(-5, -31.6) * mm, "end": v(-4.08, -31.75) * mm});
            skLineSegment(sketch, "E28.9.19.0", {"start": v(-4.08, -31.75) * mm, "end": v(-3.4, -29.8) * mm});
            skLineSegment(sketch, "E28.2.20.0", {"start": v(-0.94, -32) * mm, "end": v(-1.3, -29.97) * mm});
            skLineSegment(sketch, "E28.3.20.0", {"start": v(0, -32) * mm, "end": v(-0.94, -32) * mm});
            skLineSegment(sketch, "E28.6.20.0", {"start": v(0, -32) * mm, "end": v(0.94, -32) * mm});
            skLineSegment(sketch, "E28.9.20.0", {"start": v(0.94, -32) * mm, "end": v(1.3, -29.97) * mm});
            skLineSegment(sketch, "E28.2.21.0", {"start": v(4.08, -31.75) * mm, "end": v(3.4, -29.8) * mm});
            skLineSegment(sketch, "E28.3.21.0", {"start": v(5, -31.6) * mm, "end": v(4.08, -31.75) * mm});
            skLineSegment(sketch, "E28.6.21.0", {"start": v(5, -31.6) * mm, "end": v(5.94, -31.46) * mm});
            skLineSegment(sketch, "E28.9.21.0", {"start": v(5.94, -31.46) * mm, "end": v(5.97, -29.4) * mm});
            skLineSegment(sketch, "E28.2.22.0", {"start": v(9, -30.73) * mm, "end": v(8.03, -28.9) * mm});
            skLineSegment(sketch, "E28.3.22.0", {"start": v(9.89, -30.43) * mm, "end": v(9, -30.73) * mm});
            skLineSegment(sketch, "E28.6.22.0", {"start": v(9.89, -30.43) * mm, "end": v(10.78, -30.14) * mm});
            skLineSegment(sketch, "E28.9.22.0", {"start": v(10.78, -30.14) * mm, "end": v(10.5, -28.1) * mm});
            skLineSegment(sketch, "E28.2.23.0", {"start": v(13.69, -28.94) * mm, "end": v(12.45, -27.3) * mm});
            skLineSegment(sketch, "E28.3.23.0", {"start": v(14.53, -28.51) * mm, "end": v(13.69, -28.94) * mm});
            skLineSegment(sketch, "E28.6.23.0", {"start": v(14.53, -28.51) * mm, "end": v(15.37, -28.08) * mm});
            skLineSegment(sketch, "E28.9.23.0", {"start": v(15.37, -28.08) * mm, "end": v(14.77, -26.11) * mm});
            skLineSegment(sketch, "E28.2.24.0", {"start": v(18.05, -26.44) * mm, "end": v(16.57, -25.01) * mm});
            skLineSegment(sketch, "E28.3.24.0", {"start": v(18.8, -25.89) * mm, "end": v(18.05, -26.44) * mm});
            skLineSegment(sketch, "E28.6.24.0", {"start": v(18.8, -25.89) * mm, "end": v(19.57, -25.33) * mm});
            skLineSegment(sketch, "E28.9.24.0", {"start": v(19.57, -25.33) * mm, "end": v(18.67, -23.48) * mm});
            skLineSegment(sketch, "E28.2.25.0", {"start": v(21.96, -23.3) * mm, "end": v(20.27, -22.11) * mm});
            skLineSegment(sketch, "E28.3.25.0", {"start": v(22.63, -22.63) * mm, "end": v(21.96, -23.3) * mm});
            skLineSegment(sketch, "E28.6.25.0", {"start": v(22.63, -22.63) * mm, "end": v(23.3, -21.96) * mm});
            skLineSegment(sketch, "E28.9.25.0", {"start": v(23.3, -21.96) * mm, "end": v(22.11, -20.27) * mm});
            skLineSegment(sketch, "E28.2.26.0", {"start": v(25.33, -19.57) * mm, "end": v(23.48, -18.67) * mm});
            skLineSegment(sketch, "E28.3.26.0", {"start": v(25.89, -18.8) * mm, "end": v(25.33, -19.57) * mm});
            skLineSegment(sketch, "E28.6.26.0", {"start": v(25.89, -18.8) * mm, "end": v(26.44, -18.05) * mm});
            skLineSegment(sketch, "E28.9.26.0", {"start": v(26.44, -18.05) * mm, "end": v(25.01, -16.57) * mm});
            skLineSegment(sketch, "E28.2.27.0", {"start": v(28.08, -15.37) * mm, "end": v(26.11, -14.77) * mm});
            skLineSegment(sketch, "E28.3.27.0", {"start": v(28.51, -14.53) * mm, "end": v(28.08, -15.37) * mm});
            skLineSegment(sketch, "E28.6.27.0", {"start": v(28.51, -14.53) * mm, "end": v(28.94, -13.69) * mm});
            skLineSegment(sketch, "E28.9.27.0", {"start": v(28.94, -13.69) * mm, "end": v(27.3, -12.45) * mm});
            skLineSegment(sketch, "E28.2.28.0", {"start": v(30.14, -10.78) * mm, "end": v(28.1, -10.5) * mm});
            skLineSegment(sketch, "E28.3.28.0", {"start": v(30.43, -9.89) * mm, "end": v(30.14, -10.78) * mm});
            skLineSegment(sketch, "E28.6.28.0", {"start": v(30.43, -9.89) * mm, "end": v(30.73, -9) * mm});
            skLineSegment(sketch, "E28.9.28.0", {"start": v(30.73, -9) * mm, "end": v(28.9, -8.03) * mm});
            skLineSegment(sketch, "E28.2.29.0", {"start": v(31.46, -5.94) * mm, "end": v(29.4, -5.97) * mm});
            skLineSegment(sketch, "E28.3.29.0", {"start": v(31.6, -5) * mm, "end": v(31.46, -5.94) * mm});
            skLineSegment(sketch, "E28.6.29.0", {"start": v(31.6, -5) * mm, "end": v(31.75, -4.08) * mm});
            skLineSegment(sketch, "E28.9.29.0", {"start": v(31.75, -4.08) * mm, "end": v(29.8, -3.4) * mm});
            skLineSegment(sketch, "E28.2.30.0", {"start": v(32, -0.94) * mm, "end": v(29.97, -1.3) * mm});
            skLineSegment(sketch, "E28.3.30.0", {"start": v(32, 0) * mm, "end": v(32, -0.94) * mm});
            skLineSegment(sketch, "E28.6.30.0", {"start": v(32, 0) * mm, "end": v(32, 0.94) * mm});
            skLineSegment(sketch, "E28.9.30.0", {"start": v(32, 0.94) * mm, "end": v(29.97, 1.3) * mm});
            skLineSegment(sketch, "E28.2.31.0", {"start": v(31.75, 4.08) * mm, "end": v(29.8, 3.4) * mm});
            skLineSegment(sketch, "E28.3.31.0", {"start": v(31.6, 5) * mm, "end": v(31.75, 4.08) * mm});
            skLineSegment(sketch, "E28.6.31.0", {"start": v(31.6, 5) * mm, "end": v(31.46, 5.94) * mm});
            skLineSegment(sketch, "E28.9.31.0", {"start": v(31.46, 5.94) * mm, "end": v(29.4, 5.97) * mm});
            skLineSegment(sketch, "E28.2.32.0", {"start": v(30.73, 9) * mm, "end": v(28.9, 8.03) * mm});
            skLineSegment(sketch, "E28.3.32.0", {"start": v(30.43, 9.89) * mm, "end": v(30.73, 9) * mm});
            skLineSegment(sketch, "E28.6.32.0", {"start": v(30.43, 9.89) * mm, "end": v(30.14, 10.78) * mm});
            skLineSegment(sketch, "E28.9.32.0", {"start": v(30.14, 10.78) * mm, "end": v(28.1, 10.5) * mm});
            skLineSegment(sketch, "E28.2.33.0", {"start": v(28.94, 13.69) * mm, "end": v(27.3, 12.45) * mm});
            skLineSegment(sketch, "E28.3.33.0", {"start": v(28.51, 14.53) * mm, "end": v(28.94, 13.69) * mm});
            skLineSegment(sketch, "E28.6.33.0", {"start": v(28.51, 14.53) * mm, "end": v(28.08, 15.37) * mm});
            skLineSegment(sketch, "E28.9.33.0", {"start": v(28.08, 15.37) * mm, "end": v(26.11, 14.77) * mm});
            skLineSegment(sketch, "E28.2.34.0", {"start": v(26.44, 18.05) * mm, "end": v(25.01, 16.57) * mm});
            skLineSegment(sketch, "E28.3.34.0", {"start": v(25.89, 18.8) * mm, "end": v(26.44, 18.05) * mm});
            skLineSegment(sketch, "E28.6.34.0", {"start": v(25.89, 18.8) * mm, "end": v(25.33, 19.57) * mm});
            skLineSegment(sketch, "E28.9.34.0", {"start": v(25.33, 19.57) * mm, "end": v(23.48, 18.67) * mm});
            skLineSegment(sketch, "E28.2.35.0", {"start": v(23.3, 21.96) * mm, "end": v(22.11, 20.27) * mm});
            skLineSegment(sketch, "E28.3.35.0", {"start": v(22.63, 22.63) * mm, "end": v(23.3, 21.96) * mm});
            skLineSegment(sketch, "E28.6.35.0", {"start": v(22.63, 22.63) * mm, "end": v(21.96, 23.3) * mm});
            skLineSegment(sketch, "E28.9.35.0", {"start": v(21.96, 23.3) * mm, "end": v(20.27, 22.11) * mm});
            skLineSegment(sketch, "E28.2.36.0", {"start": v(19.57, 25.33) * mm, "end": v(18.67, 23.48) * mm});
            skLineSegment(sketch, "E28.3.36.0", {"start": v(18.8, 25.89) * mm, "end": v(19.57, 25.33) * mm});
            skLineSegment(sketch, "E28.6.36.0", {"start": v(18.8, 25.89) * mm, "end": v(18.05, 26.44) * mm});
            skLineSegment(sketch, "E28.9.36.0", {"start": v(18.05, 26.44) * mm, "end": v(16.57, 25.01) * mm});
            skLineSegment(sketch, "E28.2.37.0", {"start": v(15.37, 28.08) * mm, "end": v(14.77, 26.11) * mm});
            skLineSegment(sketch, "E28.3.37.0", {"start": v(14.53, 28.51) * mm, "end": v(15.37, 28.08) * mm});
            skLineSegment(sketch, "E28.6.37.0", {"start": v(14.53, 28.51) * mm, "end": v(13.69, 28.94) * mm});
            skLineSegment(sketch, "E28.9.37.0", {"start": v(13.69, 28.94) * mm, "end": v(12.45, 27.3) * mm});
            skLineSegment(sketch, "E28.2.38.0", {"start": v(10.78, 30.14) * mm, "end": v(10.5, 28.1) * mm});
            skLineSegment(sketch, "E28.3.38.0", {"start": v(9.89, 30.43) * mm, "end": v(10.78, 30.14) * mm});
            skLineSegment(sketch, "E28.6.38.0", {"start": v(9.89, 30.43) * mm, "end": v(9, 30.73) * mm});
            skLineSegment(sketch, "E28.9.38.0", {"start": v(9, 30.73) * mm, "end": v(8.03, 28.9) * mm});
            skLineSegment(sketch, "E28.2.39.0", {"start": v(5.94, 31.46) * mm, "end": v(5.97, 29.4) * mm});
            skLineSegment(sketch, "E28.3.39.0", {"start": v(5, 31.6) * mm, "end": v(5.94, 31.46) * mm});
            skLineSegment(sketch, "E28.6.39.0", {"start": v(5, 31.6) * mm, "end": v(4.08, 31.75) * mm});
            skLineSegment(sketch, "E28.9.39.0", {"start": v(4.08, 31.75) * mm, "end": v(3.4, 29.8) * mm});
            skSolve(sketch);
        }
        {
            var Q0;
            Q0 = qSketchRegion(id + "F14", true);
            extrude(context, id + "F15", {"entities" : qUnion([Q0]), "operationType" : NewBodyOperationType.ADD, "depth" : 4 * mm, "offsetDistance" : 25 * mm});
        }
        {
            var Q0;
            Q0=makeQuery(id+"F7.opExtrude","CAP_FACE",FACE,{"disambiguationData":[OSD([sQuery(id+"F0.wireOp",EDGE,"E0")])],"isStart":false});
            var sketch = newSketch(context, id + "F16", { "sketchPlane" : qUnion([Q0])});
            skCircle(sketch, "E29", {"center": v(40, 0) * mm, "radius": 7.5 * mm});
            skLineSegment(sketch, "E30", {"start": v(40, 0) * mm, "end": v(40, 7.5) * mm, "construction": true});
            skLineSegment(sketch, "E31", {"start": v(38.68, 7.38) * mm, "end": v(39.06, 9.5) * mm});
            skLineSegment(sketch, "E32", {"start": v(39.06, 9.5) * mm, "end": v(40.94, 9.5) * mm});
            skLineSegment(sketch, "E33.MirrorCS", {"start": v(41.32, 7.38) * mm, "end": v(40.94, 9.5) * mm});
            skLineSegment(sketch, "E34.1.0", {"start": v(34.6, 5.2) * mm, "end": v(33.65, 7.13) * mm});
            skLineSegment(sketch, "E34.1.1", {"start": v(33.65, 7.13) * mm, "end": v(35.18, 8.24) * mm});
            skLineSegment(sketch, "E34.1.2", {"start": v(36.72, 6.75) * mm, "end": v(35.18, 8.24) * mm});
            skLineSegment(sketch, "E34.2.0", {"start": v(32.57, 1.03) * mm, "end": v(30.67, 2.04) * mm});
            skLineSegment(sketch, "E34.2.1", {"start": v(30.67, 2.04) * mm, "end": v(31.26, 3.83) * mm});
            skLineSegment(sketch, "E34.2.2", {"start": v(33.38, 3.53) * mm, "end": v(31.26, 3.83) * mm});
            skLineSegment(sketch, "E35.1.3.0", {"start": v(33.38, -3.53) * mm, "end": v(31.26, -3.83) * mm});
            skLineSegment(sketch, "E35.3.3.0", {"start": v(31.26, -3.83) * mm, "end": v(30.67, -2.04) * mm});
            skLineSegment(sketch, "E35.6.3.0", {"start": v(32.57, -1.03) * mm, "end": v(30.67, -2.04) * mm});
            skLineSegment(sketch, "E35.1.4.0", {"start": v(36.72, -6.75) * mm, "end": v(35.18, -8.24) * mm});
            skLineSegment(sketch, "E35.3.4.0", {"start": v(35.18, -8.24) * mm, "end": v(33.65, -7.13) * mm});
            skLineSegment(sketch, "E35.6.4.0", {"start": v(34.6, -5.2) * mm, "end": v(33.65, -7.13) * mm});
            skLineSegment(sketch, "E35.1.5.0", {"start": v(41.32, -7.38) * mm, "end": v(40.94, -9.5) * mm});
            skLineSegment(sketch, "E35.3.5.0", {"start": v(40.94, -9.5) * mm, "end": v(39.06, -9.5) * mm});
            skLineSegment(sketch, "E35.6.5.0", {"start": v(38.68, -7.38) * mm, "end": v(39.06, -9.5) * mm});
            skLineSegment(sketch, "E35.1.6.0", {"start": v(45.4, -5.2) * mm, "end": v(46.35, -7.13) * mm});
            skLineSegment(sketch, "E35.3.6.0", {"start": v(46.35, -7.13) * mm, "end": v(44.82, -8.24) * mm});
            skLineSegment(sketch, "E35.6.6.0", {"start": v(43.28, -6.75) * mm, "end": v(44.82, -8.24) * mm});
            skLineSegment(sketch, "E35.1.7.0", {"start": v(47.43, -1.03) * mm, "end": v(49.33, -2.04) * mm});
            skLineSegment(sketch, "E35.3.7.0", {"start": v(49.33, -2.04) * mm, "end": v(48.74, -3.83) * mm});
            skLineSegment(sketch, "E35.6.7.0", {"start": v(46.62, -3.53) * mm, "end": v(48.74, -3.83) * mm});
            skLineSegment(sketch, "E35.1.8.0", {"start": v(46.62, 3.53) * mm, "end": v(48.74, 3.83) * mm});
            skLineSegment(sketch, "E35.3.8.0", {"start": v(48.74, 3.83) * mm, "end": v(49.33, 2.04) * mm});
            skLineSegment(sketch, "E35.6.8.0", {"start": v(47.43, 1.03) * mm, "end": v(49.33, 2.04) * mm});
            skLineSegment(sketch, "E35.1.9.0", {"start": v(43.28, 6.75) * mm, "end": v(44.82, 8.24) * mm});
            skLineSegment(sketch, "E35.3.9.0", {"start": v(44.82, 8.24) * mm, "end": v(46.35, 7.13) * mm});
            skLineSegment(sketch, "E35.6.9.0", {"start": v(45.4, 5.2) * mm, "end": v(46.35, 7.13) * mm});
            skSolve(sketch);
        }
        {
            var Q0;
            Q0 = qSketchRegion(id + "F16", true);
            extrude(context, id + "F17", {"entities" : qUnion([Q0]), "operationType" : NewBodyOperationType.ADD, "depth" : 4 * mm, "offsetDistance" : 25 * mm});
        }
        {
            var Q0;
            Q0=makeQuery(id+"F17.opExtrude","CAP_FACE",FACE,{"disambiguationData":[OSD([sQuery(id+"F16.wireOp",EDGE,"E29"),sQuery(id+"F16.wireOp",EDGE,"E31"),sQuery(id+"F16.wireOp",EDGE,"E32"),sQuery(id+"F16.wireOp",EDGE,"E33.MirrorCS"),sQuery(id+"F16.wireOp",EDGE,"E34.1.0"),sQuery(id+"F16.wireOp",EDGE,"E34.1.1"),sQuery(id+"F16.wireOp",EDGE,"E34.1.2"),sQuery(id+"F16.wireOp",EDGE,"E34.2.0"),sQuery(id+"F16.wireOp",EDGE,"E34.2.1"),sQuery(id+"F16.wireOp",EDGE,"E34.2.2"),sQuery(id+"F16.wireOp",EDGE,"E35.1.3.0"),sQuery(id+"F16.wireOp",EDGE,"E35.3.3.0"),sQuery(id+"F16.wireOp",EDGE,"E35.6.3.0"),sQuery(id+"F16.wireOp",EDGE,"E35.1.4.0"),sQuery(id+"F16.wireOp",EDGE,"E35.3.4.0"),sQuery(id+"F16.wireOp",EDGE,"E35.6.4.0"),sQuery(id+"F16.wireOp",EDGE,"E35.1.5.0"),sQuery(id+"F16.wireOp",EDGE,"E35.3.5.0"),sQuery(id+"F16.wireOp",EDGE,"E35.6.5.0"),sQuery(id+"F16.wireOp",EDGE,"E35.1.6.0"),sQuery(id+"F16.wireOp",EDGE,"E35.3.6.0"),sQuery(id+"F16.wireOp",EDGE,"E35.6.6.0"),sQuery(id+"F16.wireOp",EDGE,"E35.1.7.0"),sQuery(id+"F16.wireOp",EDGE,"E35.3.7.0"),sQuery(id+"F16.wireOp",EDGE,"E35.6.7.0"),sQuery(id+"F16.wireOp",EDGE,"E35.1.8.0"),sQuery(id+"F16.wireOp",EDGE,"E35.3.8.0"),sQuery(id+"F16.wireOp",EDGE,"E35.6.8.0"),sQuery(id+"F16.wireOp",EDGE,"E35.1.9.0"),sQuery(id+"F16.wireOp",EDGE,"E35.3.9.0"),sQuery(id+"F16.wireOp",EDGE,"E35.6.9.0")])],"isStart":false});
            var sketch = newSketch(context, id + "F18", { "sketchPlane" : qUnion([Q0])});
            skCircle(sketch, "E36.0", {"center": v(40, 0) * mm, "radius": 3 * mm});
            skSolve(sketch);
        }
        {
            var Q0;
            Q0 = qSketchRegion(id + "F18", true);
            extrude(context, id + "F19", {"entities" : qUnion([Q0]), "operationType" : NewBodyOperationType.ADD, "depth" : 2 * mm, "offsetDistance" : 25 * mm});
        }
        {
            var Q0;
            Q0=makeQuery(id+"F19.opExtrude","CAP_FACE",FACE,{"disambiguationData":[OSD([sQuery(id+"F18.wireOp",EDGE,"E36.0")])],"isStart":false});
            var sketch = newSketch(context, id + "F20", { "sketchPlane" : qUnion([Q0])});
            skCircle(sketch, "E37", {"center": v(0, 0) * mm, "radius": 98 * mm});
            skCircle(sketch, "E38.0", {"center": v(0, 0) * mm, "radius": 5 * mm});
            skSolve(sketch);
        }
        {
            var Q0;
            Q0 = qSketchRegion(id + "F20", true);
            extrude(context, id + "F21", {"entities" : qUnion([Q0]), "depth" : 1 * mm, "offsetDistance" : 25 * mm});
        }
        {
            var Q0;
            Q0=makeQuery(id+"F21.opExtrude","SWEPT_BODY",BODY,{"disambiguationData":[OSD([sQuery(id+"F20.wireOp",EDGE,"E37"),sQuery(id+"F20.wireOp",EDGE,"E38.0")])]});
            var Q1;
            Q1=makeQuery(id+"F1.opExtrude","SWEPT_BODY",BODY,{"disambiguationData":[OSD([sQuery(id+"F0.wireOp",EDGE,"E0")])]});
            booleanBodies(context, id + "F22", {"operationType" : BooleanOperationType.SUBTRACTION, "tools" : qUnion([Q0]), "targets" : qUnion([Q1]), "keepTools" : true});
        }
        {
            var Q0;
            Q0=makeQuery(id+"F21.opExtrude","CAP_FACE",FACE,{"disambiguationData":[OSD([sQuery(id+"F20.wireOp",EDGE,"E37"),sQuery(id+"F20.wireOp",EDGE,"E38.0")])],"isStart":true});
            var sketch = newSketch(context, id + "F23", { "sketchPlane" : qUnion([Q0])});
            skCircle(sketch, "E39.0.0", {"center": v(-40, 0) * mm, "radius": 3 * mm});
            skCircle(sketch, "E40", {"center": v(-40, 0) * mm, "radius": 5 * mm});
            skSolve(sketch);
        }
        {
            var Q0;
            Q0 = qSketchRegion(id + "F23", true);
            extrude(context, id + "F24", {"entities" : qUnion([Q0]), "operationType" : NewBodyOperationType.ADD, "endBound" : BoundingType.UP_TO_NEXT, "depth" : 25 * mm, "offsetDistance" : 25 * mm});
        }
        {
            var Q0;
            Q0=makeQuery(id+"F21.opExtrude","CAP_FACE",FACE,{"disambiguationData":[OSD([sQuery(id+"F20.wireOp",EDGE,"E37"),sQuery(id+"F20.wireOp",EDGE,"E38.0")])],"isStart":false});
            var sketch = newSketch(context, id + "F25", { "sketchPlane" : qUnion([Q0])});
            skLineSegment(sketch, "E41.bottom", {"start": v(1.5, 91) * mm, "end": v(-1.5, 91) * mm});
            skLineSegment(sketch, "E41.top", {"start": v(1.5, 62) * mm, "end": v(-1.5, 62) * mm});
            skLineSegment(sketch, "E41.left", {"start": v(1.5, 91) * mm, "end": v(1.5, 62) * mm});
            skLineSegment(sketch, "E41.right", {"start": v(-1.5, 91) * mm, "end": v(-1.5, 62) * mm});
            skPoint(sketch, "E41.middle", {"position": v(0, 76.5) * mm});
            skLineSegment(sketch, "E42.1.0", {"start": v(-46.8, 78.06) * mm, "end": v(-32.3, 52.94) * mm});
            skLineSegment(sketch, "E42.1.1", {"start": v(-44.2, 79.56) * mm, "end": v(-29.7, 54.44) * mm});
            skLineSegment(sketch, "E42.1.2", {"start": v(-44.2, 79.56) * mm, "end": v(-46.8, 78.06) * mm});
            skLineSegment(sketch, "E42.1.3", {"start": v(-29.7, 54.44) * mm, "end": v(-32.3, 52.94) * mm});
            skLineSegment(sketch, "E42.2.0", {"start": v(-79.56, 44.2) * mm, "end": v(-54.44, 29.7) * mm});
            skLineSegment(sketch, "E42.2.1", {"start": v(-78.06, 46.8) * mm, "end": v(-52.94, 32.3) * mm});
            skLineSegment(sketch, "E42.2.2", {"start": v(-78.06, 46.8) * mm, "end": v(-79.56, 44.2) * mm});
            skLineSegment(sketch, "E42.2.3", {"start": v(-52.94, 32.3) * mm, "end": v(-54.44, 29.7) * mm});
            skPoint(sketch, "E42.center", {"position": v(0, 0) * mm});
            skLineSegment(sketch, "E43.2.3.0", {"start": v(-91, -1.5) * mm, "end": v(-62, -1.5) * mm});
            skLineSegment(sketch, "E43.3.3.0", {"start": v(-91, 1.5) * mm, "end": v(-62, 1.5) * mm});
            skLineSegment(sketch, "E43.6.3.0", {"start": v(-91, 1.5) * mm, "end": v(-91, -1.5) * mm});
            skLineSegment(sketch, "E43.9.3.0", {"start": v(-62, 1.5) * mm, "end": v(-62, -1.5) * mm});
            skLineSegment(sketch, "E43.2.4.0", {"start": v(-78.06, -46.8) * mm, "end": v(-52.94, -32.3) * mm});
            skLineSegment(sketch, "E43.3.4.0", {"start": v(-79.56, -44.2) * mm, "end": v(-54.44, -29.7) * mm});
            skLineSegment(sketch, "E43.6.4.0", {"start": v(-79.56, -44.2) * mm, "end": v(-78.06, -46.8) * mm});
            skLineSegment(sketch, "E43.9.4.0", {"start": v(-54.44, -29.7) * mm, "end": v(-52.94, -32.3) * mm});
            skLineSegment(sketch, "E43.2.5.0", {"start": v(-44.2, -79.56) * mm, "end": v(-29.7, -54.44) * mm});
            skLineSegment(sketch, "E43.3.5.0", {"start": v(-46.8, -78.06) * mm, "end": v(-32.3, -52.94) * mm});
            skLineSegment(sketch, "E43.6.5.0", {"start": v(-46.8, -78.06) * mm, "end": v(-44.2, -79.56) * mm});
            skLineSegment(sketch, "E43.9.5.0", {"start": v(-32.3, -52.94) * mm, "end": v(-29.7, -54.44) * mm});
            skLineSegment(sketch, "E43.2.6.0", {"start": v(1.5, -91) * mm, "end": v(1.5, -62) * mm});
            skLineSegment(sketch, "E43.3.6.0", {"start": v(-1.5, -91) * mm, "end": v(-1.5, -62) * mm});
            skLineSegment(sketch, "E43.6.6.0", {"start": v(-1.5, -91) * mm, "end": v(1.5, -91) * mm});
            skLineSegment(sketch, "E43.9.6.0", {"start": v(-1.5, -62) * mm, "end": v(1.5, -62) * mm});
            skLineSegment(sketch, "E43.2.7.0", {"start": v(46.8, -78.06) * mm, "end": v(32.3, -52.94) * mm});
            skLineSegment(sketch, "E43.3.7.0", {"start": v(44.2, -79.56) * mm, "end": v(29.7, -54.44) * mm});
            skLineSegment(sketch, "E43.6.7.0", {"start": v(44.2, -79.56) * mm, "end": v(46.8, -78.06) * mm});
            skLineSegment(sketch, "E43.9.7.0", {"start": v(29.7, -54.44) * mm, "end": v(32.3, -52.94) * mm});
            skLineSegment(sketch, "E43.2.8.0", {"start": v(79.56, -44.2) * mm, "end": v(54.44, -29.7) * mm});
            skLineSegment(sketch, "E43.3.8.0", {"start": v(78.06, -46.8) * mm, "end": v(52.94, -32.3) * mm});
            skLineSegment(sketch, "E43.6.8.0", {"start": v(78.06, -46.8) * mm, "end": v(79.56, -44.2) * mm});
            skLineSegment(sketch, "E43.9.8.0", {"start": v(52.94, -32.3) * mm, "end": v(54.44, -29.7) * mm});
            skLineSegment(sketch, "E43.2.9.0", {"start": v(91, 1.5) * mm, "end": v(62, 1.5) * mm});
            skLineSegment(sketch, "E43.3.9.0", {"start": v(91, -1.5) * mm, "end": v(62, -1.5) * mm});
            skLineSegment(sketch, "E43.6.9.0", {"start": v(91, -1.5) * mm, "end": v(91, 1.5) * mm});
            skLineSegment(sketch, "E43.9.9.0", {"start": v(62, -1.5) * mm, "end": v(62, 1.5) * mm});
            skLineSegment(sketch, "E43.2.10.0", {"start": v(78.06, 46.8) * mm, "end": v(52.94, 32.3) * mm});
            skLineSegment(sketch, "E43.3.10.0", {"start": v(79.56, 44.2) * mm, "end": v(54.44, 29.7) * mm});
            skLineSegment(sketch, "E43.6.10.0", {"start": v(79.56, 44.2) * mm, "end": v(78.06, 46.8) * mm});
            skLineSegment(sketch, "E43.9.10.0", {"start": v(54.44, 29.7) * mm, "end": v(52.94, 32.3) * mm});
            skLineSegment(sketch, "E43.2.11.0", {"start": v(44.2, 79.56) * mm, "end": v(29.7, 54.44) * mm});
            skLineSegment(sketch, "E43.3.11.0", {"start": v(46.8, 78.06) * mm, "end": v(32.3, 52.94) * mm});
            skLineSegment(sketch, "E43.6.11.0", {"start": v(46.8, 78.06) * mm, "end": v(44.2, 79.56) * mm});
            skLineSegment(sketch, "E43.9.11.0", {"start": v(32.3, 52.94) * mm, "end": v(29.7, 54.44) * mm});
            skSolve(sketch);
        }
        {
            var Q0;
            Q0 = qSketchRegion(id + "F25", true);
            extrude(context, id + "F26", {"entities" : qUnion([Q0]), "operationType" : NewBodyOperationType.REMOVE, "oppositeDirection" : true, "depth" : 0.5 * mm, "offsetDistance" : 25 * mm});
        }
        {
            var Q0;
            Q0=makeQuery(id+"F21.opExtrude","CAP_FACE",FACE,{"disambiguationData":[OSD([sQuery(id+"F20.wireOp",EDGE,"E37"),sQuery(id+"F20.wireOp",EDGE,"E38.0")])],"isStart":false});
            var sketch = newSketch(context, id + "F27", { "sketchPlane" : qUnion([Q0])});
            skLineSegment(sketch, "E44.bottom", {"start": v(0.75, 90.5) * mm, "end": v(-0.75, 90.5) * mm});
            skLineSegment(sketch, "E44.top", {"start": v(0.75, 78.5) * mm, "end": v(-0.75, 78.5) * mm});
            skLineSegment(sketch, "E44.left", {"start": v(0.75, 90.5) * mm, "end": v(0.75, 78.5) * mm});
            skLineSegment(sketch, "E44.right", {"start": v(-0.75, 90.5) * mm, "end": v(-0.75, 78.5) * mm});
            skPoint(sketch, "E44.middle", {"position": v(0, 84.5) * mm});
            skLineSegment(sketch, "E45.1.0", {"start": v(-8.71, 90.08) * mm, "end": v(-7.46, 78.15) * mm});
            skLineSegment(sketch, "E45.1.1", {"start": v(-10.2, 89.93) * mm, "end": v(-8.95, 78) * mm});
            skLineSegment(sketch, "E45.1.2", {"start": v(-8.71, 90.08) * mm, "end": v(-10.2, 89.93) * mm});
            skLineSegment(sketch, "E45.1.3", {"start": v(-7.46, 78.15) * mm, "end": v(-8.95, 78) * mm});
            skLineSegment(sketch, "E45.2.0", {"start": v(-18.08, 88.68) * mm, "end": v(-15.59, 76.94) * mm});
            skLineSegment(sketch, "E45.2.1", {"start": v(-19.55, 88.37) * mm, "end": v(-17.05, 76.63) * mm});
            skLineSegment(sketch, "E45.2.2", {"start": v(-18.08, 88.68) * mm, "end": v(-19.55, 88.37) * mm});
            skLineSegment(sketch, "E45.2.3", {"start": v(-15.59, 76.94) * mm, "end": v(-17.05, 76.63) * mm});
            skPoint(sketch, "E45.center", {"position": v(0, 0) * mm});
            skLineSegment(sketch, "E46.2.3.0", {"start": v(-27.25, 86.3) * mm, "end": v(-23.54, 74.89) * mm});
            skLineSegment(sketch, "E46.3.3.0", {"start": v(-28.68, 85.84) * mm, "end": v(-24.97, 74.43) * mm});
            skLineSegment(sketch, "E46.6.3.0", {"start": v(-27.25, 86.3) * mm, "end": v(-28.68, 85.84) * mm});
            skLineSegment(sketch, "E46.9.3.0", {"start": v(-23.54, 74.89) * mm, "end": v(-24.97, 74.43) * mm});
            skLineSegment(sketch, "E46.2.4.0", {"start": v(-36.12, 82.98) * mm, "end": v(-31.24, 72.02) * mm});
            skLineSegment(sketch, "E46.3.4.0", {"start": v(-37.5, 82.37) * mm, "end": v(-32.61, 71.4) * mm});
            skLineSegment(sketch, "E46.6.4.0", {"start": v(-36.12, 82.98) * mm, "end": v(-37.5, 82.37) * mm});
            skLineSegment(sketch, "E46.9.4.0", {"start": v(-31.24, 72.02) * mm, "end": v(-32.61, 71.4) * mm});
            skLineSegment(sketch, "E46.2.5.0", {"start": v(-44.6, 78.75) * mm, "end": v(-38.6, 68.36) * mm});
            skLineSegment(sketch, "E46.3.5.0", {"start": v(-45.9, 78) * mm, "end": v(-39.9, 67.6) * mm});
            skLineSegment(sketch, "E46.6.5.0", {"start": v(-44.6, 78.75) * mm, "end": v(-45.9, 78) * mm});
            skLineSegment(sketch, "E46.9.5.0", {"start": v(-38.6, 68.36) * mm, "end": v(-39.9, 67.6) * mm});
            skLineSegment(sketch, "E46.2.6.0", {"start": v(-52.59, 73.66) * mm, "end": v(-45.53, 63.95) * mm});
            skLineSegment(sketch, "E46.3.6.0", {"start": v(-53.8, 72.78) * mm, "end": v(-46.75, 63.07) * mm});
            skLineSegment(sketch, "E46.6.6.0", {"start": v(-52.59, 73.66) * mm, "end": v(-53.8, 72.78) * mm});
            skLineSegment(sketch, "E46.9.6.0", {"start": v(-45.53, 63.95) * mm, "end": v(-46.75, 63.07) * mm});
            skLineSegment(sketch, "E46.2.7.0", {"start": v(-60, 67.76) * mm, "end": v(-51.97, 58.84) * mm});
            skLineSegment(sketch, "E46.3.7.0", {"start": v(-61.11, 66.75) * mm, "end": v(-53.08, 57.84) * mm});
            skLineSegment(sketch, "E46.6.7.0", {"start": v(-60, 67.76) * mm, "end": v(-61.11, 66.75) * mm});
            skLineSegment(sketch, "E46.9.7.0", {"start": v(-51.97, 58.84) * mm, "end": v(-53.08, 57.84) * mm});
            skLineSegment(sketch, "E46.2.8.0", {"start": v(-66.75, 61.11) * mm, "end": v(-57.84, 53.08) * mm});
            skLineSegment(sketch, "E46.3.8.0", {"start": v(-67.76, 60) * mm, "end": v(-58.84, 51.97) * mm});
            skLineSegment(sketch, "E46.6.8.0", {"start": v(-66.75, 61.11) * mm, "end": v(-67.76, 60) * mm});
            skLineSegment(sketch, "E46.9.8.0", {"start": v(-57.84, 53.08) * mm, "end": v(-58.84, 51.97) * mm});
            skLineSegment(sketch, "E46.2.9.0", {"start": v(-72.78, 53.8) * mm, "end": v(-63.07, 46.75) * mm});
            skLineSegment(sketch, "E46.3.9.0", {"start": v(-73.66, 52.59) * mm, "end": v(-63.95, 45.53) * mm});
            skLineSegment(sketch, "E46.6.9.0", {"start": v(-72.78, 53.8) * mm, "end": v(-73.66, 52.59) * mm});
            skLineSegment(sketch, "E46.9.9.0", {"start": v(-63.07, 46.75) * mm, "end": v(-63.95, 45.53) * mm});
            skLineSegment(sketch, "E46.2.10.0", {"start": v(-78, 45.9) * mm, "end": v(-67.6, 39.9) * mm});
            skLineSegment(sketch, "E46.3.10.0", {"start": v(-78.75, 44.6) * mm, "end": v(-68.36, 38.6) * mm});
            skLineSegment(sketch, "E46.6.10.0", {"start": v(-78, 45.9) * mm, "end": v(-78.75, 44.6) * mm});
            skLineSegment(sketch, "E46.9.10.0", {"start": v(-67.6, 39.9) * mm, "end": v(-68.36, 38.6) * mm});
            skLineSegment(sketch, "E46.2.11.0", {"start": v(-82.37, 37.5) * mm, "end": v(-71.4, 32.61) * mm});
            skLineSegment(sketch, "E46.3.11.0", {"start": v(-82.98, 36.12) * mm, "end": v(-72.02, 31.24) * mm});
            skLineSegment(sketch, "E46.6.11.0", {"start": v(-82.37, 37.5) * mm, "end": v(-82.98, 36.12) * mm});
            skLineSegment(sketch, "E46.9.11.0", {"start": v(-71.4, 32.61) * mm, "end": v(-72.02, 31.24) * mm});
            skLineSegment(sketch, "E46.2.12.0", {"start": v(-85.84, 28.68) * mm, "end": v(-74.43, 24.97) * mm});
            skLineSegment(sketch, "E46.3.12.0", {"start": v(-86.3, 27.25) * mm, "end": v(-74.89, 23.54) * mm});
            skLineSegment(sketch, "E46.6.12.0", {"start": v(-85.84, 28.68) * mm, "end": v(-86.3, 27.25) * mm});
            skLineSegment(sketch, "E46.9.12.0", {"start": v(-74.43, 24.97) * mm, "end": v(-74.89, 23.54) * mm});
            skLineSegment(sketch, "E46.2.13.0", {"start": v(-88.37, 19.55) * mm, "end": v(-76.63, 17.05) * mm});
            skLineSegment(sketch, "E46.3.13.0", {"start": v(-88.68, 18.08) * mm, "end": v(-76.94, 15.59) * mm});
            skLineSegment(sketch, "E46.6.13.0", {"start": v(-88.37, 19.55) * mm, "end": v(-88.68, 18.08) * mm});
            skLineSegment(sketch, "E46.9.13.0", {"start": v(-76.63, 17.05) * mm, "end": v(-76.94, 15.59) * mm});
            skLineSegment(sketch, "E46.2.14.0", {"start": v(-89.93, 10.2) * mm, "end": v(-78, 8.95) * mm});
            skLineSegment(sketch, "E46.3.14.0", {"start": v(-90.08, 8.71) * mm, "end": v(-78.15, 7.46) * mm});
            skLineSegment(sketch, "E46.6.14.0", {"start": v(-89.93, 10.2) * mm, "end": v(-90.08, 8.71) * mm});
            skLineSegment(sketch, "E46.9.14.0", {"start": v(-78, 8.95) * mm, "end": v(-78.15, 7.46) * mm});
            skLineSegment(sketch, "E46.2.15.0", {"start": v(-90.5, 0.75) * mm, "end": v(-78.5, 0.75) * mm});
            skLineSegment(sketch, "E46.3.15.0", {"start": v(-90.5, -0.75) * mm, "end": v(-78.5, -0.75) * mm});
            skLineSegment(sketch, "E46.6.15.0", {"start": v(-90.5, 0.75) * mm, "end": v(-90.5, -0.75) * mm});
            skLineSegment(sketch, "E46.9.15.0", {"start": v(-78.5, 0.75) * mm, "end": v(-78.5, -0.75) * mm});
            skLineSegment(sketch, "E46.2.16.0", {"start": v(-90.08, -8.71) * mm, "end": v(-78.15, -7.46) * mm});
            skLineSegment(sketch, "E46.3.16.0", {"start": v(-89.93, -10.2) * mm, "end": v(-78, -8.95) * mm});
            skLineSegment(sketch, "E46.6.16.0", {"start": v(-90.08, -8.71) * mm, "end": v(-89.93, -10.2) * mm});
            skLineSegment(sketch, "E46.9.16.0", {"start": v(-78.15, -7.46) * mm, "end": v(-78, -8.95) * mm});
            skLineSegment(sketch, "E46.2.17.0", {"start": v(-88.68, -18.08) * mm, "end": v(-76.94, -15.59) * mm});
            skLineSegment(sketch, "E46.3.17.0", {"start": v(-88.37, -19.55) * mm, "end": v(-76.63, -17.05) * mm});
            skLineSegment(sketch, "E46.6.17.0", {"start": v(-88.68, -18.08) * mm, "end": v(-88.37, -19.55) * mm});
            skLineSegment(sketch, "E46.9.17.0", {"start": v(-76.94, -15.59) * mm, "end": v(-76.63, -17.05) * mm});
            skLineSegment(sketch, "E46.2.18.0", {"start": v(-86.3, -27.25) * mm, "end": v(-74.89, -23.54) * mm});
            skLineSegment(sketch, "E46.3.18.0", {"start": v(-85.84, -28.68) * mm, "end": v(-74.43, -24.97) * mm});
            skLineSegment(sketch, "E46.6.18.0", {"start": v(-86.3, -27.25) * mm, "end": v(-85.84, -28.68) * mm});
            skLineSegment(sketch, "E46.9.18.0", {"start": v(-74.89, -23.54) * mm, "end": v(-74.43, -24.97) * mm});
            skLineSegment(sketch, "E46.2.19.0", {"start": v(-82.98, -36.12) * mm, "end": v(-72.02, -31.24) * mm});
            skLineSegment(sketch, "E46.3.19.0", {"start": v(-82.37, -37.5) * mm, "end": v(-71.4, -32.61) * mm});
            skLineSegment(sketch, "E46.6.19.0", {"start": v(-82.98, -36.12) * mm, "end": v(-82.37, -37.5) * mm});
            skLineSegment(sketch, "E46.9.19.0", {"start": v(-72.02, -31.24) * mm, "end": v(-71.4, -32.61) * mm});
            skLineSegment(sketch, "E46.2.20.0", {"start": v(-78.75, -44.6) * mm, "end": v(-68.36, -38.6) * mm});
            skLineSegment(sketch, "E46.3.20.0", {"start": v(-78, -45.9) * mm, "end": v(-67.6, -39.9) * mm});
            skLineSegment(sketch, "E46.6.20.0", {"start": v(-78.75, -44.6) * mm, "end": v(-78, -45.9) * mm});
            skLineSegment(sketch, "E46.9.20.0", {"start": v(-68.36, -38.6) * mm, "end": v(-67.6, -39.9) * mm});
            skLineSegment(sketch, "E46.2.21.0", {"start": v(-73.66, -52.59) * mm, "end": v(-63.95, -45.53) * mm});
            skLineSegment(sketch, "E46.3.21.0", {"start": v(-72.78, -53.8) * mm, "end": v(-63.07, -46.75) * mm});
            skLineSegment(sketch, "E46.6.21.0", {"start": v(-73.66, -52.59) * mm, "end": v(-72.78, -53.8) * mm});
            skLineSegment(sketch, "E46.9.21.0", {"start": v(-63.95, -45.53) * mm, "end": v(-63.07, -46.75) * mm});
            skLineSegment(sketch, "E46.2.22.0", {"start": v(-67.76, -60) * mm, "end": v(-58.84, -51.97) * mm});
            skLineSegment(sketch, "E46.3.22.0", {"start": v(-66.75, -61.11) * mm, "end": v(-57.84, -53.08) * mm});
            skLineSegment(sketch, "E46.6.22.0", {"start": v(-67.76, -60) * mm, "end": v(-66.75, -61.11) * mm});
            skLineSegment(sketch, "E46.9.22.0", {"start": v(-58.84, -51.97) * mm, "end": v(-57.84, -53.08) * mm});
            skLineSegment(sketch, "E46.2.23.0", {"start": v(-61.11, -66.75) * mm, "end": v(-53.08, -57.84) * mm});
            skLineSegment(sketch, "E46.3.23.0", {"start": v(-60, -67.76) * mm, "end": v(-51.97, -58.84) * mm});
            skLineSegment(sketch, "E46.6.23.0", {"start": v(-61.11, -66.75) * mm, "end": v(-60, -67.76) * mm});
            skLineSegment(sketch, "E46.9.23.0", {"start": v(-53.08, -57.84) * mm, "end": v(-51.97, -58.84) * mm});
            skLineSegment(sketch, "E46.2.24.0", {"start": v(-53.8, -72.78) * mm, "end": v(-46.75, -63.07) * mm});
            skLineSegment(sketch, "E46.3.24.0", {"start": v(-52.59, -73.66) * mm, "end": v(-45.53, -63.95) * mm});
            skLineSegment(sketch, "E46.6.24.0", {"start": v(-53.8, -72.78) * mm, "end": v(-52.59, -73.66) * mm});
            skLineSegment(sketch, "E46.9.24.0", {"start": v(-46.75, -63.07) * mm, "end": v(-45.53, -63.95) * mm});
            skLineSegment(sketch, "E46.2.25.0", {"start": v(-45.9, -78) * mm, "end": v(-39.9, -67.6) * mm});
            skLineSegment(sketch, "E46.3.25.0", {"start": v(-44.6, -78.75) * mm, "end": v(-38.6, -68.36) * mm});
            skLineSegment(sketch, "E46.6.25.0", {"start": v(-45.9, -78) * mm, "end": v(-44.6, -78.75) * mm});
            skLineSegment(sketch, "E46.9.25.0", {"start": v(-39.9, -67.6) * mm, "end": v(-38.6, -68.36) * mm});
            skLineSegment(sketch, "E46.2.26.0", {"start": v(-37.5, -82.37) * mm, "end": v(-32.61, -71.4) * mm});
            skLineSegment(sketch, "E46.3.26.0", {"start": v(-36.12, -82.98) * mm, "end": v(-31.24, -72.02) * mm});
            skLineSegment(sketch, "E46.6.26.0", {"start": v(-37.5, -82.37) * mm, "end": v(-36.12, -82.98) * mm});
            skLineSegment(sketch, "E46.9.26.0", {"start": v(-32.61, -71.4) * mm, "end": v(-31.24, -72.02) * mm});
            skLineSegment(sketch, "E46.2.27.0", {"start": v(-28.68, -85.84) * mm, "end": v(-24.97, -74.43) * mm});
            skLineSegment(sketch, "E46.3.27.0", {"start": v(-27.25, -86.3) * mm, "end": v(-23.54, -74.89) * mm});
            skLineSegment(sketch, "E46.6.27.0", {"start": v(-28.68, -85.84) * mm, "end": v(-27.25, -86.3) * mm});
            skLineSegment(sketch, "E46.9.27.0", {"start": v(-24.97, -74.43) * mm, "end": v(-23.54, -74.89) * mm});
            skLineSegment(sketch, "E46.2.28.0", {"start": v(-19.55, -88.37) * mm, "end": v(-17.05, -76.63) * mm});
            skLineSegment(sketch, "E46.3.28.0", {"start": v(-18.08, -88.68) * mm, "end": v(-15.59, -76.94) * mm});
            skLineSegment(sketch, "E46.6.28.0", {"start": v(-19.55, -88.37) * mm, "end": v(-18.08, -88.68) * mm});
            skLineSegment(sketch, "E46.9.28.0", {"start": v(-17.05, -76.63) * mm, "end": v(-15.59, -76.94) * mm});
            skLineSegment(sketch, "E46.2.29.0", {"start": v(-10.2, -89.93) * mm, "end": v(-8.95, -78) * mm});
            skLineSegment(sketch, "E46.3.29.0", {"start": v(-8.71, -90.08) * mm, "end": v(-7.46, -78.15) * mm});
            skLineSegment(sketch, "E46.6.29.0", {"start": v(-10.2, -89.93) * mm, "end": v(-8.71, -90.08) * mm});
            skLineSegment(sketch, "E46.9.29.0", {"start": v(-8.95, -78) * mm, "end": v(-7.46, -78.15) * mm});
            skLineSegment(sketch, "E46.2.30.0", {"start": v(-0.75, -90.5) * mm, "end": v(-0.75, -78.5) * mm});
            skLineSegment(sketch, "E46.3.30.0", {"start": v(0.75, -90.5) * mm, "end": v(0.75, -78.5) * mm});
            skLineSegment(sketch, "E46.6.30.0", {"start": v(-0.75, -90.5) * mm, "end": v(0.75, -90.5) * mm});
            skLineSegment(sketch, "E46.9.30.0", {"start": v(-0.75, -78.5) * mm, "end": v(0.75, -78.5) * mm});
            skLineSegment(sketch, "E46.2.31.0", {"start": v(8.71, -90.08) * mm, "end": v(7.46, -78.15) * mm});
            skLineSegment(sketch, "E46.3.31.0", {"start": v(10.2, -89.93) * mm, "end": v(8.95, -78) * mm});
            skLineSegment(sketch, "E46.6.31.0", {"start": v(8.71, -90.08) * mm, "end": v(10.2, -89.93) * mm});
            skLineSegment(sketch, "E46.9.31.0", {"start": v(7.46, -78.15) * mm, "end": v(8.95, -78) * mm});
            skLineSegment(sketch, "E46.2.32.0", {"start": v(18.08, -88.68) * mm, "end": v(15.59, -76.94) * mm});
            skLineSegment(sketch, "E46.3.32.0", {"start": v(19.55, -88.37) * mm, "end": v(17.05, -76.63) * mm});
            skLineSegment(sketch, "E46.6.32.0", {"start": v(18.08, -88.68) * mm, "end": v(19.55, -88.37) * mm});
            skLineSegment(sketch, "E46.9.32.0", {"start": v(15.59, -76.94) * mm, "end": v(17.05, -76.63) * mm});
            skLineSegment(sketch, "E46.2.33.0", {"start": v(27.25, -86.3) * mm, "end": v(23.54, -74.89) * mm});
            skLineSegment(sketch, "E46.3.33.0", {"start": v(28.68, -85.84) * mm, "end": v(24.97, -74.43) * mm});
            skLineSegment(sketch, "E46.6.33.0", {"start": v(27.25, -86.3) * mm, "end": v(28.68, -85.84) * mm});
            skLineSegment(sketch, "E46.9.33.0", {"start": v(23.54, -74.89) * mm, "end": v(24.97, -74.43) * mm});
            skLineSegment(sketch, "E46.2.34.0", {"start": v(36.12, -82.98) * mm, "end": v(31.24, -72.02) * mm});
            skLineSegment(sketch, "E46.3.34.0", {"start": v(37.5, -82.37) * mm, "end": v(32.61, -71.4) * mm});
            skLineSegment(sketch, "E46.6.34.0", {"start": v(36.12, -82.98) * mm, "end": v(37.5, -82.37) * mm});
            skLineSegment(sketch, "E46.9.34.0", {"start": v(31.24, -72.02) * mm, "end": v(32.61, -71.4) * mm});
            skLineSegment(sketch, "E46.2.35.0", {"start": v(44.6, -78.75) * mm, "end": v(38.6, -68.36) * mm});
            skLineSegment(sketch, "E46.3.35.0", {"start": v(45.9, -78) * mm, "end": v(39.9, -67.6) * mm});
            skLineSegment(sketch, "E46.6.35.0", {"start": v(44.6, -78.75) * mm, "end": v(45.9, -78) * mm});
            skLineSegment(sketch, "E46.9.35.0", {"start": v(38.6, -68.36) * mm, "end": v(39.9, -67.6) * mm});
            skLineSegment(sketch, "E46.2.36.0", {"start": v(52.59, -73.66) * mm, "end": v(45.53, -63.95) * mm});
            skLineSegment(sketch, "E46.3.36.0", {"start": v(53.8, -72.78) * mm, "end": v(46.75, -63.07) * mm});
            skLineSegment(sketch, "E46.6.36.0", {"start": v(52.59, -73.66) * mm, "end": v(53.8, -72.78) * mm});
            skLineSegment(sketch, "E46.9.36.0", {"start": v(45.53, -63.95) * mm, "end": v(46.75, -63.07) * mm});
            skLineSegment(sketch, "E46.2.37.0", {"start": v(60, -67.76) * mm, "end": v(51.97, -58.84) * mm});
            skLineSegment(sketch, "E46.3.37.0", {"start": v(61.11, -66.75) * mm, "end": v(53.08, -57.84) * mm});
            skLineSegment(sketch, "E46.6.37.0", {"start": v(60, -67.76) * mm, "end": v(61.11, -66.75) * mm});
            skLineSegment(sketch, "E46.9.37.0", {"start": v(51.97, -58.84) * mm, "end": v(53.08, -57.84) * mm});
            skLineSegment(sketch, "E46.2.38.0", {"start": v(66.75, -61.11) * mm, "end": v(57.84, -53.08) * mm});
            skLineSegment(sketch, "E46.3.38.0", {"start": v(67.76, -60) * mm, "end": v(58.84, -51.97) * mm});
            skLineSegment(sketch, "E46.6.38.0", {"start": v(66.75, -61.11) * mm, "end": v(67.76, -60) * mm});
            skLineSegment(sketch, "E46.9.38.0", {"start": v(57.84, -53.08) * mm, "end": v(58.84, -51.97) * mm});
            skLineSegment(sketch, "E46.2.39.0", {"start": v(72.78, -53.8) * mm, "end": v(63.07, -46.75) * mm});
            skLineSegment(sketch, "E46.3.39.0", {"start": v(73.66, -52.59) * mm, "end": v(63.95, -45.53) * mm});
            skLineSegment(sketch, "E46.6.39.0", {"start": v(72.78, -53.8) * mm, "end": v(73.66, -52.59) * mm});
            skLineSegment(sketch, "E46.9.39.0", {"start": v(63.07, -46.75) * mm, "end": v(63.95, -45.53) * mm});
            skLineSegment(sketch, "E46.2.40.0", {"start": v(78, -45.9) * mm, "end": v(67.6, -39.9) * mm});
            skLineSegment(sketch, "E46.3.40.0", {"start": v(78.75, -44.6) * mm, "end": v(68.36, -38.6) * mm});
            skLineSegment(sketch, "E46.6.40.0", {"start": v(78, -45.9) * mm, "end": v(78.75, -44.6) * mm});
            skLineSegment(sketch, "E46.9.40.0", {"start": v(67.6, -39.9) * mm, "end": v(68.36, -38.6) * mm});
            skLineSegment(sketch, "E46.2.41.0", {"start": v(82.37, -37.5) * mm, "end": v(71.4, -32.61) * mm});
            skLineSegment(sketch, "E46.3.41.0", {"start": v(82.98, -36.12) * mm, "end": v(72.02, -31.24) * mm});
            skLineSegment(sketch, "E46.6.41.0", {"start": v(82.37, -37.5) * mm, "end": v(82.98, -36.12) * mm});
            skLineSegment(sketch, "E46.9.41.0", {"start": v(71.4, -32.61) * mm, "end": v(72.02, -31.24) * mm});
            skLineSegment(sketch, "E46.2.42.0", {"start": v(85.84, -28.68) * mm, "end": v(74.43, -24.97) * mm});
            skLineSegment(sketch, "E46.3.42.0", {"start": v(86.3, -27.25) * mm, "end": v(74.89, -23.54) * mm});
            skLineSegment(sketch, "E46.6.42.0", {"start": v(85.84, -28.68) * mm, "end": v(86.3, -27.25) * mm});
            skLineSegment(sketch, "E46.9.42.0", {"start": v(74.43, -24.97) * mm, "end": v(74.89, -23.54) * mm});
            skLineSegment(sketch, "E46.2.43.0", {"start": v(88.37, -19.55) * mm, "end": v(76.63, -17.05) * mm});
            skLineSegment(sketch, "E46.3.43.0", {"start": v(88.68, -18.08) * mm, "end": v(76.94, -15.59) * mm});
            skLineSegment(sketch, "E46.6.43.0", {"start": v(88.37, -19.55) * mm, "end": v(88.68, -18.08) * mm});
            skLineSegment(sketch, "E46.9.43.0", {"start": v(76.63, -17.05) * mm, "end": v(76.94, -15.59) * mm});
            skLineSegment(sketch, "E46.2.44.0", {"start": v(89.93, -10.2) * mm, "end": v(78, -8.95) * mm});
            skLineSegment(sketch, "E46.3.44.0", {"start": v(90.08, -8.71) * mm, "end": v(78.15, -7.46) * mm});
            skLineSegment(sketch, "E46.6.44.0", {"start": v(89.93, -10.2) * mm, "end": v(90.08, -8.71) * mm});
            skLineSegment(sketch, "E46.9.44.0", {"start": v(78, -8.95) * mm, "end": v(78.15, -7.46) * mm});
            skLineSegment(sketch, "E46.2.45.0", {"start": v(90.5, -0.75) * mm, "end": v(78.5, -0.75) * mm});
            skLineSegment(sketch, "E46.3.45.0", {"start": v(90.5, 0.75) * mm, "end": v(78.5, 0.75) * mm});
            skLineSegment(sketch, "E46.6.45.0", {"start": v(90.5, -0.75) * mm, "end": v(90.5, 0.75) * mm});
            skLineSegment(sketch, "E46.9.45.0", {"start": v(78.5, -0.75) * mm, "end": v(78.5, 0.75) * mm});
            skLineSegment(sketch, "E46.2.46.0", {"start": v(90.08, 8.71) * mm, "end": v(78.15, 7.46) * mm});
            skLineSegment(sketch, "E46.3.46.0", {"start": v(89.93, 10.2) * mm, "end": v(78, 8.95) * mm});
            skLineSegment(sketch, "E46.6.46.0", {"start": v(90.08, 8.71) * mm, "end": v(89.93, 10.2) * mm});
            skLineSegment(sketch, "E46.9.46.0", {"start": v(78.15, 7.46) * mm, "end": v(78, 8.95) * mm});
            skLineSegment(sketch, "E46.2.47.0", {"start": v(88.68, 18.08) * mm, "end": v(76.94, 15.59) * mm});
            skLineSegment(sketch, "E46.3.47.0", {"start": v(88.37, 19.55) * mm, "end": v(76.63, 17.05) * mm});
            skLineSegment(sketch, "E46.6.47.0", {"start": v(88.68, 18.08) * mm, "end": v(88.37, 19.55) * mm});
            skLineSegment(sketch, "E46.9.47.0", {"start": v(76.94, 15.59) * mm, "end": v(76.63, 17.05) * mm});
            skLineSegment(sketch, "E46.2.48.0", {"start": v(86.3, 27.25) * mm, "end": v(74.89, 23.54) * mm});
            skLineSegment(sketch, "E46.3.48.0", {"start": v(85.84, 28.68) * mm, "end": v(74.43, 24.97) * mm});
            skLineSegment(sketch, "E46.6.48.0", {"start": v(86.3, 27.25) * mm, "end": v(85.84, 28.68) * mm});
            skLineSegment(sketch, "E46.9.48.0", {"start": v(74.89, 23.54) * mm, "end": v(74.43, 24.97) * mm});
            skLineSegment(sketch, "E46.2.49.0", {"start": v(82.98, 36.12) * mm, "end": v(72.02, 31.24) * mm});
            skLineSegment(sketch, "E46.3.49.0", {"start": v(82.37, 37.5) * mm, "end": v(71.4, 32.61) * mm});
            skLineSegment(sketch, "E46.6.49.0", {"start": v(82.98, 36.12) * mm, "end": v(82.37, 37.5) * mm});
            skLineSegment(sketch, "E46.9.49.0", {"start": v(72.02, 31.24) * mm, "end": v(71.4, 32.61) * mm});
            skLineSegment(sketch, "E46.2.50.0", {"start": v(78.75, 44.6) * mm, "end": v(68.36, 38.6) * mm});
            skLineSegment(sketch, "E46.3.50.0", {"start": v(78, 45.9) * mm, "end": v(67.6, 39.9) * mm});
            skLineSegment(sketch, "E46.6.50.0", {"start": v(78.75, 44.6) * mm, "end": v(78, 45.9) * mm});
            skLineSegment(sketch, "E46.9.50.0", {"start": v(68.36, 38.6) * mm, "end": v(67.6, 39.9) * mm});
            skLineSegment(sketch, "E46.2.51.0", {"start": v(73.66, 52.59) * mm, "end": v(63.95, 45.53) * mm});
            skLineSegment(sketch, "E46.3.51.0", {"start": v(72.78, 53.8) * mm, "end": v(63.07, 46.75) * mm});
            skLineSegment(sketch, "E46.6.51.0", {"start": v(73.66, 52.59) * mm, "end": v(72.78, 53.8) * mm});
            skLineSegment(sketch, "E46.9.51.0", {"start": v(63.95, 45.53) * mm, "end": v(63.07, 46.75) * mm});
            skLineSegment(sketch, "E46.2.52.0", {"start": v(67.76, 60) * mm, "end": v(58.84, 51.97) * mm});
            skLineSegment(sketch, "E46.3.52.0", {"start": v(66.75, 61.11) * mm, "end": v(57.84, 53.08) * mm});
            skLineSegment(sketch, "E46.6.52.0", {"start": v(67.76, 60) * mm, "end": v(66.75, 61.11) * mm});
            skLineSegment(sketch, "E46.9.52.0", {"start": v(58.84, 51.97) * mm, "end": v(57.84, 53.08) * mm});
            skLineSegment(sketch, "E46.2.53.0", {"start": v(61.11, 66.75) * mm, "end": v(53.08, 57.84) * mm});
            skLineSegment(sketch, "E46.3.53.0", {"start": v(60, 67.76) * mm, "end": v(51.97, 58.84) * mm});
            skLineSegment(sketch, "E46.6.53.0", {"start": v(61.11, 66.75) * mm, "end": v(60, 67.76) * mm});
            skLineSegment(sketch, "E46.9.53.0", {"start": v(53.08, 57.84) * mm, "end": v(51.97, 58.84) * mm});
            skLineSegment(sketch, "E46.2.54.0", {"start": v(53.8, 72.78) * mm, "end": v(46.75, 63.07) * mm});
            skLineSegment(sketch, "E46.3.54.0", {"start": v(52.59, 73.66) * mm, "end": v(45.53, 63.95) * mm});
            skLineSegment(sketch, "E46.6.54.0", {"start": v(53.8, 72.78) * mm, "end": v(52.59, 73.66) * mm});
            skLineSegment(sketch, "E46.9.54.0", {"start": v(46.75, 63.07) * mm, "end": v(45.53, 63.95) * mm});
            skLineSegment(sketch, "E46.2.55.0", {"start": v(45.9, 78) * mm, "end": v(39.9, 67.6) * mm});
            skLineSegment(sketch, "E46.3.55.0", {"start": v(44.6, 78.75) * mm, "end": v(38.6, 68.36) * mm});
            skLineSegment(sketch, "E46.6.55.0", {"start": v(45.9, 78) * mm, "end": v(44.6, 78.75) * mm});
            skLineSegment(sketch, "E46.9.55.0", {"start": v(39.9, 67.6) * mm, "end": v(38.6, 68.36) * mm});
            skLineSegment(sketch, "E46.2.56.0", {"start": v(37.5, 82.37) * mm, "end": v(32.61, 71.4) * mm});
            skLineSegment(sketch, "E46.3.56.0", {"start": v(36.12, 82.98) * mm, "end": v(31.24, 72.02) * mm});
            skLineSegment(sketch, "E46.6.56.0", {"start": v(37.5, 82.37) * mm, "end": v(36.12, 82.98) * mm});
            skLineSegment(sketch, "E46.9.56.0", {"start": v(32.61, 71.4) * mm, "end": v(31.24, 72.02) * mm});
            skLineSegment(sketch, "E46.2.57.0", {"start": v(28.68, 85.84) * mm, "end": v(24.97, 74.43) * mm});
            skLineSegment(sketch, "E46.3.57.0", {"start": v(27.25, 86.3) * mm, "end": v(23.54, 74.89) * mm});
            skLineSegment(sketch, "E46.6.57.0", {"start": v(28.68, 85.84) * mm, "end": v(27.25, 86.3) * mm});
            skLineSegment(sketch, "E46.9.57.0", {"start": v(24.97, 74.43) * mm, "end": v(23.54, 74.89) * mm});
            skLineSegment(sketch, "E46.2.58.0", {"start": v(19.55, 88.37) * mm, "end": v(17.05, 76.63) * mm});
            skLineSegment(sketch, "E46.3.58.0", {"start": v(18.08, 88.68) * mm, "end": v(15.59, 76.94) * mm});
            skLineSegment(sketch, "E46.6.58.0", {"start": v(19.55, 88.37) * mm, "end": v(18.08, 88.68) * mm});
            skLineSegment(sketch, "E46.9.58.0", {"start": v(17.05, 76.63) * mm, "end": v(15.59, 76.94) * mm});
            skLineSegment(sketch, "E46.2.59.0", {"start": v(10.2, 89.93) * mm, "end": v(8.95, 78) * mm});
            skLineSegment(sketch, "E46.3.59.0", {"start": v(8.71, 90.08) * mm, "end": v(7.46, 78.15) * mm});
            skLineSegment(sketch, "E46.6.59.0", {"start": v(10.2, 89.93) * mm, "end": v(8.71, 90.08) * mm});
            skLineSegment(sketch, "E46.9.59.0", {"start": v(8.95, 78) * mm, "end": v(7.46, 78.15) * mm});
            skSolve(sketch);
        }
        {
            var Q0;
            Q0 = qSketchRegion(id + "F27", true);
            extrude(context, id + "F28", {"entities" : qUnion([Q0]), "operationType" : NewBodyOperationType.REMOVE, "oppositeDirection" : true, "depth" : 0.2 * mm, "offsetDistance" : 25 * mm});
        }
        {
            var Q0;
            Q0=makeQuery(id+"F26.boolean.opBoolean","COPY",FACE,{"derivedFrom":makeQuery(id+"F26.opExtrude","CAP_FACE",FACE,{"disambiguationData":[OSD([sQuery(id+"F25.wireOp",EDGE,"E41.bottom"),sQuery(id+"F25.wireOp",EDGE,"E41.top"),sQuery(id+"F25.wireOp",EDGE,"E41.left"),sQuery(id+"F25.wireOp",EDGE,"E41.right")])],"isStart":false})});
            extrude(context, id + "F29", {"entities" : qUnion([Q0]), "depth" : 1 * mm, "offsetDistance" : 25 * mm});
        }
        {
            var Q0;
            Q0=makeQuery(id+"F28.boolean.opBoolean","COPY",FACE,{"derivedFrom":makeQuery(id+"F28.opExtrude","CAP_FACE",FACE,{"disambiguationData":[OSD([sQuery(id+"F27.wireOp",EDGE,"E46.2.59.0"),sQuery(id+"F27.wireOp",EDGE,"E46.3.59.0"),sQuery(id+"F27.wireOp",EDGE,"E46.6.59.0"),sQuery(id+"F27.wireOp",EDGE,"E46.9.59.0")])],"isStart":false})});
            extrude(context, id + "F30", {"entities" : qUnion([Q0]), "depth" : 0.4 * mm, "offsetDistance" : 25 * mm});
        }
        {
            var Q0;
            Q0=makeQuery(id+"F15.opExtrude","CAP_FACE",FACE,{"disambiguationData":[OSD([sQuery(id+"F14.wireOp",EDGE,"E21.0"),sQuery(id+"F14.wireOp",EDGE,"E22"),sQuery(id+"F14.wireOp",EDGE,"E23"),sQuery(id+"F14.wireOp",EDGE,"E24"),sQuery(id+"F14.wireOp",EDGE,"E25.MirrorCS"),sQuery(id+"F14.wireOp",EDGE,"E26.MirrorCS"),sQuery(id+"F14.wireOp",EDGE,"E27.1.0"),sQuery(id+"F14.wireOp",EDGE,"E27.1.1"),sQuery(id+"F14.wireOp",EDGE,"E27.1.2"),sQuery(id+"F14.wireOp",EDGE,"E27.1.3"),sQuery(id+"F14.wireOp",EDGE,"E27.2.0"),sQuery(id+"F14.wireOp",EDGE,"E27.2.1"),sQuery(id+"F14.wireOp",EDGE,"E27.2.2"),sQuery(id+"F14.wireOp",EDGE,"E27.2.3"),sQuery(id+"F14.wireOp",EDGE,"E28.2.3.0"),sQuery(id+"F14.wireOp",EDGE,"E28.3.3.0"),sQuery(id+"F14.wireOp",EDGE,"E28.6.3.0"),sQuery(id+"F14.wireOp",EDGE,"E28.9.3.0"),sQuery(id+"F14.wireOp",EDGE,"E28.2.4.0"),sQuery(id+"F14.wireOp",EDGE,"E28.3.4.0"),sQuery(id+"F14.wireOp",EDGE,"E28.6.4.0"),sQuery(id+"F14.wireOp",EDGE,"E28.9.4.0"),sQuery(id+"F14.wireOp",EDGE,"E28.2.5.0"),sQuery(id+"F14.wireOp",EDGE,"E28.3.5.0"),sQuery(id+"F14.wireOp",EDGE,"E28.6.5.0"),sQuery(id+"F14.wireOp",EDGE,"E28.9.5.0"),sQuery(id+"F14.wireOp",EDGE,"E28.2.6.0"),sQuery(id+"F14.wireOp",EDGE,"E28.3.6.0"),sQuery(id+"F14.wireOp",EDGE,"E28.6.6.0"),sQuery(id+"F14.wireOp",EDGE,"E28.9.6.0"),sQuery(id+"F14.wireOp",EDGE,"E28.2.7.0"),sQuery(id+"F14.wireOp",EDGE,"E28.3.7.0"),sQuery(id+"F14.wireOp",EDGE,"E28.6.7.0"),sQuery(id+"F14.wireOp",EDGE,"E28.9.7.0"),sQuery(id+"F14.wireOp",EDGE,"E28.2.8.0"),sQuery(id+"F14.wireOp",EDGE,"E28.3.8.0"),sQuery(id+"F14.wireOp",EDGE,"E28.6.8.0"),sQuery(id+"F14.wireOp",EDGE,"E28.9.8.0"),sQuery(id+"F14.wireOp",EDGE,"E28.2.9.0"),sQuery(id+"F14.wireOp",EDGE,"E28.3.9.0"),sQuery(id+"F14.wireOp",EDGE,"E28.6.9.0"),sQuery(id+"F14.wireOp",EDGE,"E28.9.9.0"),sQuery(id+"F14.wireOp",EDGE,"E28.2.10.0"),sQuery(id+"F14.wireOp",EDGE,"E28.3.10.0"),sQuery(id+"F14.wireOp",EDGE,"E28.6.10.0"),sQuery(id+"F14.wireOp",EDGE,"E28.9.10.0"),sQuery(id+"F14.wireOp",EDGE,"E28.2.11.0"),sQuery(id+"F14.wireOp",EDGE,"E28.3.11.0"),sQuery(id+"F14.wireOp",EDGE,"E28.6.11.0"),sQuery(id+"F14.wireOp",EDGE,"E28.9.11.0"),sQuery(id+"F14.wireOp",EDGE,"E28.2.12.0"),sQuery(id+"F14.wireOp",EDGE,"E28.3.12.0"),sQuery(id+"F14.wireOp",EDGE,"E28.6.12.0"),sQuery(id+"F14.wireOp",EDGE,"E28.9.12.0"),sQuery(id+"F14.wireOp",EDGE,"E28.2.13.0"),sQuery(id+"F14.wireOp",EDGE,"E28.3.13.0"),sQuery(id+"F14.wireOp",EDGE,"E28.6.13.0"),sQuery(id+"F14.wireOp",EDGE,"E28.9.13.0"),sQuery(id+"F14.wireOp",EDGE,"E28.2.14.0"),sQuery(id+"F14.wireOp",EDGE,"E28.3.14.0"),sQuery(id+"F14.wireOp",EDGE,"E28.6.14.0"),sQuery(id+"F14.wireOp",EDGE,"E28.9.14.0"),sQuery(id+"F14.wireOp",EDGE,"E28.2.15.0"),sQuery(id+"F14.wireOp",EDGE,"E28.3.15.0"),sQuery(id+"F14.wireOp",EDGE,"E28.6.15.0"),sQuery(id+"F14.wireOp",EDGE,"E28.9.15.0"),sQuery(id+"F14.wireOp",EDGE,"E28.2.16.0"),sQuery(id+"F14.wireOp",EDGE,"E28.3.16.0"),sQuery(id+"F14.wireOp",EDGE,"E28.6.16.0"),sQuery(id+"F14.wireOp",EDGE,"E28.9.16.0"),sQuery(id+"F14.wireOp",EDGE,"E28.2.17.0"),sQuery(id+"F14.wireOp",EDGE,"E28.3.17.0"),sQuery(id+"F14.wireOp",EDGE,"E28.6.17.0"),sQuery(id+"F14.wireOp",EDGE,"E28.9.17.0"),sQuery(id+"F14.wireOp",EDGE,"E28.2.18.0"),sQuery(id+"F14.wireOp",EDGE,"E28.3.18.0"),sQuery(id+"F14.wireOp",EDGE,"E28.6.18.0"),sQuery(id+"F14.wireOp",EDGE,"E28.9.18.0"),sQuery(id+"F14.wireOp",EDGE,"E28.2.19.0"),sQuery(id+"F14.wireOp",EDGE,"E28.3.19.0"),sQuery(id+"F14.wireOp",EDGE,"E28.6.19.0"),sQuery(id+"F14.wireOp",EDGE,"E28.9.19.0"),sQuery(id+"F14.wireOp",EDGE,"E28.2.20.0"),sQuery(id+"F14.wireOp",EDGE,"E28.3.20.0"),sQuery(id+"F14.wireOp",EDGE,"E28.6.20.0"),sQuery(id+"F14.wireOp",EDGE,"E28.9.20.0"),sQuery(id+"F14.wireOp",EDGE,"E28.2.21.0"),sQuery(id+"F14.wireOp",EDGE,"E28.3.21.0"),sQuery(id+"F14.wireOp",EDGE,"E28.6.21.0"),sQuery(id+"F14.wireOp",EDGE,"E28.9.21.0"),sQuery(id+"F14.wireOp",EDGE,"E28.2.22.0"),sQuery(id+"F14.wireOp",EDGE,"E28.3.22.0"),sQuery(id+"F14.wireOp",EDGE,"E28.6.22.0"),sQuery(id+"F14.wireOp",EDGE,"E28.9.22.0"),sQuery(id+"F14.wireOp",EDGE,"E28.2.23.0"),sQuery(id+"F14.wireOp",EDGE,"E28.3.23.0"),sQuery(id+"F14.wireOp",EDGE,"E28.6.23.0"),sQuery(id+"F14.wireOp",EDGE,"E28.9.23.0"),sQuery(id+"F14.wireOp",EDGE,"E28.2.24.0"),sQuery(id+"F14.wireOp",EDGE,"E28.3.24.0"),sQuery(id+"F14.wireOp",EDGE,"E28.6.24.0"),sQuery(id+"F14.wireOp",EDGE,"E28.9.24.0"),sQuery(id+"F14.wireOp",EDGE,"E28.2.25.0"),sQuery(id+"F14.wireOp",EDGE,"E28.3.25.0"),sQuery(id+"F14.wireOp",EDGE,"E28.6.25.0"),sQuery(id+"F14.wireOp",EDGE,"E28.9.25.0"),sQuery(id+"F14.wireOp",EDGE,"E28.2.26.0"),sQuery(id+"F14.wireOp",EDGE,"E28.3.26.0"),sQuery(id+"F14.wireOp",EDGE,"E28.6.26.0"),sQuery(id+"F14.wireOp",EDGE,"E28.9.26.0"),sQuery(id+"F14.wireOp",EDGE,"E28.2.27.0"),sQuery(id+"F14.wireOp",EDGE,"E28.3.27.0"),sQuery(id+"F14.wireOp",EDGE,"E28.6.27.0"),sQuery(id+"F14.wireOp",EDGE,"E28.9.27.0"),sQuery(id+"F14.wireOp",EDGE,"E28.2.28.0"),sQuery(id+"F14.wireOp",EDGE,"E28.3.28.0"),sQuery(id+"F14.wireOp",EDGE,"E28.6.28.0"),sQuery(id+"F14.wireOp",EDGE,"E28.9.28.0"),sQuery(id+"F14.wireOp",EDGE,"E28.2.29.0"),sQuery(id+"F14.wireOp",EDGE,"E28.3.29.0"),sQuery(id+"F14.wireOp",EDGE,"E28.6.29.0"),sQuery(id+"F14.wireOp",EDGE,"E28.9.29.0"),sQuery(id+"F14.wireOp",EDGE,"E28.2.30.0"),sQuery(id+"F14.wireOp",EDGE,"E28.3.30.0"),sQuery(id+"F14.wireOp",EDGE,"E28.6.30.0"),sQuery(id+"F14.wireOp",EDGE,"E28.9.30.0"),sQuery(id+"F14.wireOp",EDGE,"E28.2.31.0"),sQuery(id+"F14.wireOp",EDGE,"E28.3.31.0"),sQuery(id+"F14.wireOp",EDGE,"E28.6.31.0"),sQuery(id+"F14.wireOp",EDGE,"E28.9.31.0"),sQuery(id+"F14.wireOp",EDGE,"E28.2.32.0"),sQuery(id+"F14.wireOp",EDGE,"E28.3.32.0"),sQuery(id+"F14.wireOp",EDGE,"E28.6.32.0"),sQuery(id+"F14.wireOp",EDGE,"E28.9.32.0"),sQuery(id+"F14.wireOp",EDGE,"E28.2.33.0"),sQuery(id+"F14.wireOp",EDGE,"E28.3.33.0"),sQuery(id+"F14.wireOp",EDGE,"E28.6.33.0"),sQuery(id+"F14.wireOp",EDGE,"E28.9.33.0"),sQuery(id+"F14.wireOp",EDGE,"E28.2.34.0"),sQuery(id+"F14.wireOp",EDGE,"E28.3.34.0"),sQuery(id+"F14.wireOp",EDGE,"E28.6.34.0"),sQuery(id+"F14.wireOp",EDGE,"E28.9.34.0"),sQuery(id+"F14.wireOp",EDGE,"E28.2.35.0"),sQuery(id+"F14.wireOp",EDGE,"E28.3.35.0"),sQuery(id+"F14.wireOp",EDGE,"E28.6.35.0"),sQuery(id+"F14.wireOp",EDGE,"E28.9.35.0"),sQuery(id+"F14.wireOp",EDGE,"E28.2.36.0"),sQuery(id+"F14.wireOp",EDGE,"E28.3.36.0"),sQuery(id+"F14.wireOp",EDGE,"E28.6.36.0"),sQuery(id+"F14.wireOp",EDGE,"E28.9.36.0"),sQuery(id+"F14.wireOp",EDGE,"E28.2.37.0"),sQuery(id+"F14.wireOp",EDGE,"E28.3.37.0"),sQuery(id+"F14.wireOp",EDGE,"E28.6.37.0"),sQuery(id+"F14.wireOp",EDGE,"E28.9.37.0"),sQuery(id+"F14.wireOp",EDGE,"E28.2.38.0"),sQuery(id+"F14.wireOp",EDGE,"E28.3.38.0"),sQuery(id+"F14.wireOp",EDGE,"E28.6.38.0"),sQuery(id+"F14.wireOp",EDGE,"E28.9.38.0"),sQuery(id+"F14.wireOp",EDGE,"E28.2.39.0"),sQuery(id+"F14.wireOp",EDGE,"E28.3.39.0"),sQuery(id+"F14.wireOp",EDGE,"E28.6.39.0"),sQuery(id+"F14.wireOp",EDGE,"E28.9.39.0")])],"isStart":false});
            var sketch = newSketch(context, id + "F31", { "sketchPlane" : qUnion([Q0])});
            skCircle(sketch, "E47.0", {"center": v(0, 0) * mm, "radius": 3 * mm});
            skCircle(sketch, "E48.0", {"center": v(0, 0) * mm, "radius": 5 * mm});
            skSolve(sketch);
        }
        {
            var Q0;
            Q0 = qSketchRegion(id + "F31", true);
            extrude(context, id + "F32", {"entities" : qUnion([Q0]), "operationType" : NewBodyOperationType.ADD, "depth" : 5 * mm, "offsetDistance" : 25 * mm});
        }
        {
            var Q0;
            Q0=makeQuery(id+"F32.opExtrude","CAP_FACE",FACE,{"disambiguationData":[OSD([sQuery(id+"F31.wireOp",EDGE,"E47.0"),sQuery(id+"F31.wireOp",EDGE,"E48.0")])],"isStart":false});
            var sketch = newSketch(context, id + "F33", { "sketchPlane" : qUnion([Q0])});
            skCircle(sketch, "E49.0", {"center": v(0, 0) * mm, "radius": 5 * mm});
            skCircle(sketch, "E50.0", {"center": v(0, 0) * mm, "radius": 3 * mm});
            skLineSegment(sketch, "E51", {"start": v(2.88, 4.09) * mm, "end": v(1.5, 50) * mm});
            skLineSegment(sketch, "E52", {"start": v(1.5, 50) * mm, "end": v(0, 50) * mm});
            skLineSegment(sketch, "E53.MirrorCS", {"start": v(-1.5, 50) * mm, "end": v(0, 50) * mm});
            skLineSegment(sketch, "E54.MirrorCS", {"start": v(-2.88, 4.09) * mm, "end": v(-1.5, 50) * mm});
            skSolve(sketch);
        }
        {
            var Q0;
            Q0 = qSketchRegion(id + "F33", true);
            extrude(context, id + "F34", {"entities" : qUnion([Q0]), "operationType" : NewBodyOperationType.ADD, "depth" : 1 * mm, "offsetDistance" : 25 * mm});
        }
        {
            var Q0;
            Q0=makeQuery(id+"F6.opExtrude","CAP_FACE",FACE,{"disambiguationData":[OSD([sQuery(id+"F0.wireOp",EDGE,"E0")])],"isStart":false});
            var sketch = newSketch(context, id + "F35", { "sketchPlane" : qUnion([Q0])});
            skCircle(sketch, "E55", {"center": v(0, 0) * mm, "radius": 5 * mm});
            skLineSegment(sketch, "E56", {"start": v(0, 80) * mm, "end": v(1, 80) * mm});
            skLineSegment(sketch, "E57", {"start": v(1, 80) * mm, "end": v(2, 4.58) * mm});
            skLineSegment(sketch, "E58.MirrorCS", {"start": v(0, 80) * mm, "end": v(-1, 80) * mm});
            skLineSegment(sketch, "E59.MirrorCS", {"start": v(-1, 80) * mm, "end": v(-2, 4.58) * mm});
            skSolve(sketch);
        }
        {
            var Q0;
            Q0 = qSketchRegion(id + "F35", true);
            extrude(context, id + "F36", {"entities" : qUnion([Q0]), "operationType" : NewBodyOperationType.ADD, "oppositeDirection" : true, "depth" : 1 * mm, "offsetDistance" : 25 * mm});
        }
    });
